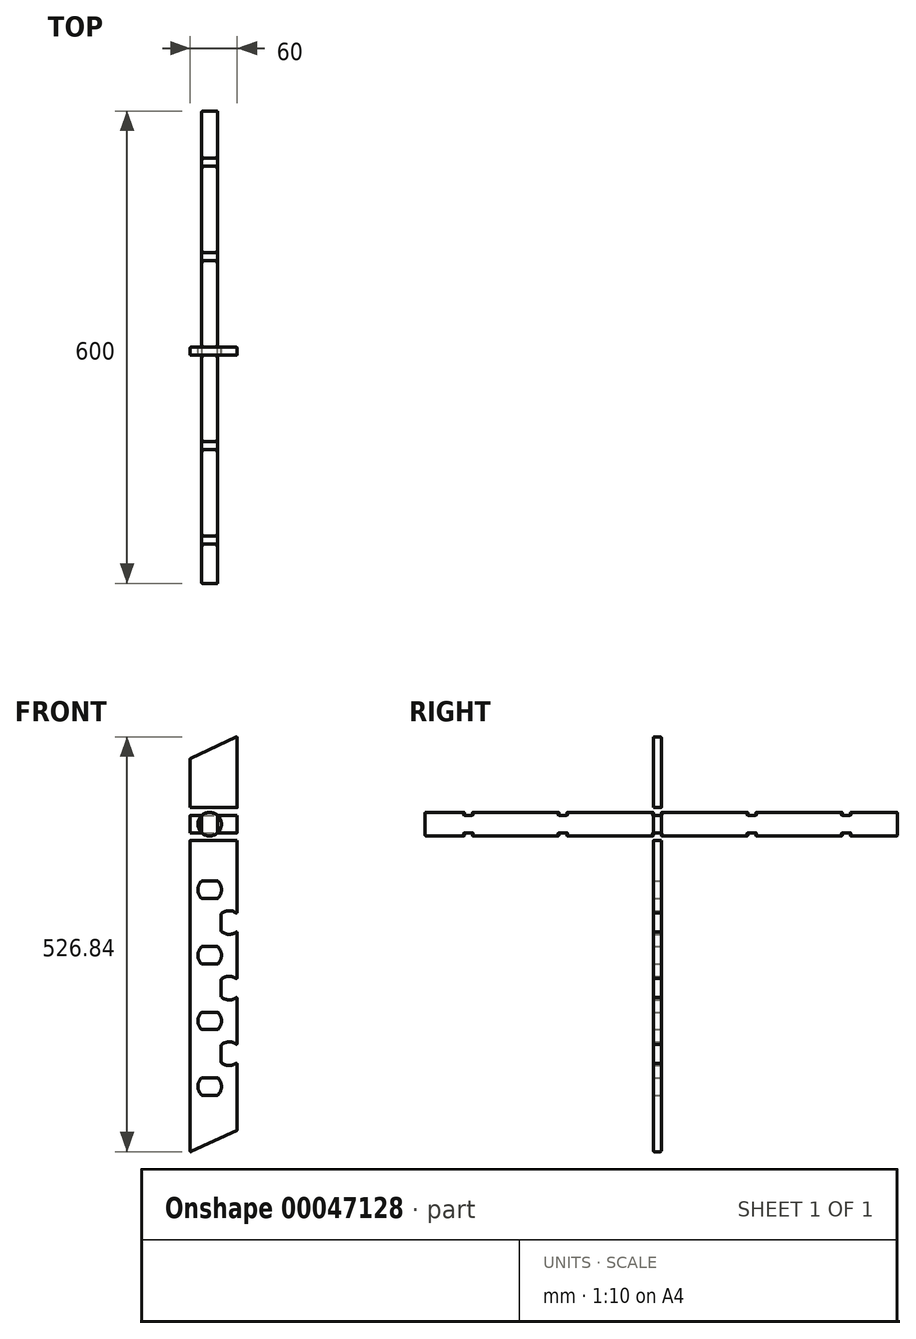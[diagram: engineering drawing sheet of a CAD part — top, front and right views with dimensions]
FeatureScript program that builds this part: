
annotation { "Feature Type Name" : "Feature", "Feature Type Description" : "" }
export const myFeature = defineFeature(function(context is Context, id is Id, definition is map)
    precondition{}
    {
        {
            var Q0;
            Q0=qCreatedBy(makeId("Front.planeOp"),FACE);
            var sketch = newSketch(context, id + "F0", { "sketchPlane" : qUnion([Q0])});
            skLineSegment(sketch, "E0.bottom", {"start": v(0, 0) * mm, "end": v(-60, 0) * mm, "construction": true});
            skLineSegment(sketch, "E0.left", {"start": v(0, 0) * mm, "end": v(0, 27.98) * mm, "construction": true});
            skLineSegment(sketch, "E1", {"start": v(0, 527.98) * mm, "end": v(-60, 500) * mm});
            skLineSegment(sketch, "E2", {"start": v(-60, 0) * mm, "end": v(0, 27.98) * mm});
            skLineSegment(sketch, "E3", {"start": v(0, 27.98) * mm, "end": v(0, 527.98) * mm});
            skLineSegment(sketch, "E4", {"start": v(-60, 500) * mm, "end": v(-60, 416.67) * mm});
            skLineSegment(sketch, "E5", {"start": v(-60, 250) * mm, "end": v(-60, 166.67) * mm});
            skLineSegment(sketch, "E6", {"start": v(-60, 83.33) * mm, "end": v(-60, 0) * mm});
            skLineSegment(sketch, "E7", {"start": v(-60, 166.67) * mm, "end": v(-60, 83.33) * mm});
            skLineSegment(sketch, "E8", {"start": v(-60, 333.33) * mm, "end": v(-60, 250) * mm});
            skLineSegment(sketch, "E9", {"start": v(-60, 416.67) * mm, "end": v(-60, 333.33) * mm});
            skLineSegment(sketch, "E10", {"start": v(-60, 416.67) * mm, "end": v(0, 416.67) * mm, "construction": true});
            skLineSegment(sketch, "E11", {"start": v(-60, 333.33) * mm, "end": v(0, 333.33) * mm, "construction": true});
            skLineSegment(sketch, "E12", {"start": v(-60, 250) * mm, "end": v(0, 250) * mm, "construction": true});
            skLineSegment(sketch, "E13", {"start": v(-60, 166.67) * mm, "end": v(0, 166.67) * mm, "construction": true});
            skLineSegment(sketch, "E14", {"start": v(-60, 83.33) * mm, "end": v(0, 83.33) * mm, "construction": true});
            skLineSegment(sketch, "E15", {"start": v(-35, 511.66) * mm, "end": v(-35, 11.66) * mm, "construction": true});
            skLineSegment(sketch, "E16", {"start": v(-45.2, 427.67) * mm, "end": v(-24.8, 427.67) * mm});
            skLineSegment(sketch, "E17", {"start": v(-24.8, 427.67) * mm, "end": v(-24.8, 405.67) * mm, "construction": true});
            skLineSegment(sketch, "E18", {"start": v(-24.8, 405.67) * mm, "end": v(-45.2, 405.67) * mm});
            skLineSegment(sketch, "E19", {"start": v(-45.2, 405.67) * mm, "end": v(-45.2, 427.67) * mm, "construction": true});
            skLineSegment(sketch, "E20", {"start": v(-45.2, 427.67) * mm, "end": v(-45.2, 427.67) * mm});
            skLineSegment(sketch, "E21", {"start": v(-45.2, 405.67) * mm, "end": v(-45.2, 405.67) * mm});
            skArc(sketch, "E22", {"start": v(-24.8, 405.67) * mm, "mid": v(-20, 416.67) * mm, "end": v(-24.8, 427.67) * mm});
            skArc(sketch, "E23", {"start": v(-45.2, 427.67) * mm, "mid": v(-50, 416.67) * mm, "end": v(-45.2, 405.67) * mm});
            skArc(sketch, "E24", {"start": v(-45.2, 427.67) * mm, "mid": v(-35, 431.67) * mm, "end": v(-24.8, 427.67) * mm, "construction": true});
            skArc(sketch, "E25", {"start": v(-24.8, 405.67) * mm, "mid": v(-35, 401.67) * mm, "end": v(-45.2, 405.67) * mm, "construction": true});
            skLineSegment(sketch, "E26", {"start": v(-45.2, 344.33) * mm, "end": v(-45.2, 344.33) * mm});
            skLineSegment(sketch, "E27", {"start": v(-45.2, 322.33) * mm, "end": v(-45.2, 344.33) * mm, "construction": true});
            skLineSegment(sketch, "E28", {"start": v(-24.8, 322.33) * mm, "end": v(-45.2, 322.33) * mm});
            skLineSegment(sketch, "E29", {"start": v(-45.2, 344.33) * mm, "end": v(-24.8, 344.33) * mm});
            skArc(sketch, "E30", {"start": v(-24.8, 322.33) * mm, "mid": v(-20, 333.33) * mm, "end": v(-24.8, 344.33) * mm});
            skArc(sketch, "E31", {"start": v(-24.8, 322.33) * mm, "mid": v(-35, 318.33) * mm, "end": v(-45.2, 322.33) * mm, "construction": true});
            skArc(sketch, "E32", {"start": v(-45.2, 344.33) * mm, "mid": v(-50, 333.33) * mm, "end": v(-45.2, 322.33) * mm});
            skLineSegment(sketch, "E33", {"start": v(-24.8, 344.33) * mm, "end": v(-24.8, 322.33) * mm, "construction": true});
            skArc(sketch, "E34", {"start": v(-45.2, 344.33) * mm, "mid": v(-35, 348.33) * mm, "end": v(-24.8, 344.33) * mm, "construction": true});
            skLineSegment(sketch, "E35", {"start": v(-45.2, 322.33) * mm, "end": v(-45.2, 322.33) * mm});
            skLineSegment(sketch, "E36", {"start": v(-45.2, 261) * mm, "end": v(-45.2, 261) * mm});
            skLineSegment(sketch, "E37", {"start": v(-45.2, 239) * mm, "end": v(-45.2, 261) * mm, "construction": true});
            skLineSegment(sketch, "E38", {"start": v(-24.8, 239) * mm, "end": v(-45.2, 239) * mm});
            skLineSegment(sketch, "E39", {"start": v(-45.2, 261) * mm, "end": v(-24.8, 261) * mm});
            skArc(sketch, "E40", {"start": v(-24.8, 239) * mm, "mid": v(-20, 250) * mm, "end": v(-24.8, 261) * mm});
            skArc(sketch, "E41", {"start": v(-24.8, 239) * mm, "mid": v(-35, 235) * mm, "end": v(-45.2, 239) * mm, "construction": true});
            skArc(sketch, "E42", {"start": v(-45.2, 261) * mm, "mid": v(-50, 250) * mm, "end": v(-45.2, 239) * mm});
            skLineSegment(sketch, "E43", {"start": v(-24.8, 261) * mm, "end": v(-24.8, 239) * mm, "construction": true});
            skArc(sketch, "E44", {"start": v(-45.2, 261) * mm, "mid": v(-35, 265) * mm, "end": v(-24.8, 261) * mm, "construction": true});
            skLineSegment(sketch, "E45", {"start": v(-45.2, 239) * mm, "end": v(-45.2, 239) * mm});
            skLineSegment(sketch, "E46", {"start": v(-45.2, 177.67) * mm, "end": v(-45.2, 177.67) * mm});
            skLineSegment(sketch, "E47", {"start": v(-45.2, 155.67) * mm, "end": v(-45.2, 177.67) * mm, "construction": true});
            skLineSegment(sketch, "E48", {"start": v(-24.8, 155.67) * mm, "end": v(-45.2, 155.67) * mm});
            skLineSegment(sketch, "E49", {"start": v(-45.2, 177.67) * mm, "end": v(-24.8, 177.67) * mm});
            skArc(sketch, "E50", {"start": v(-24.8, 155.67) * mm, "mid": v(-20, 166.67) * mm, "end": v(-24.8, 177.67) * mm});
            skArc(sketch, "E51", {"start": v(-24.8, 155.67) * mm, "mid": v(-35, 151.67) * mm, "end": v(-45.2, 155.67) * mm, "construction": true});
            skArc(sketch, "E52", {"start": v(-45.2, 177.67) * mm, "mid": v(-50, 166.67) * mm, "end": v(-45.2, 155.67) * mm});
            skLineSegment(sketch, "E53", {"start": v(-24.8, 177.67) * mm, "end": v(-24.8, 155.67) * mm, "construction": true});
            skArc(sketch, "E54", {"start": v(-45.2, 177.67) * mm, "mid": v(-35, 181.67) * mm, "end": v(-24.8, 177.67) * mm, "construction": true});
            skLineSegment(sketch, "E55", {"start": v(-45.2, 155.67) * mm, "end": v(-45.2, 155.67) * mm});
            skLineSegment(sketch, "E56", {"start": v(-45.2, 94.33) * mm, "end": v(-45.2, 94.33) * mm});
            skLineSegment(sketch, "E57", {"start": v(-45.2, 72.33) * mm, "end": v(-45.2, 94.33) * mm, "construction": true});
            skLineSegment(sketch, "E58", {"start": v(-24.8, 72.33) * mm, "end": v(-45.2, 72.33) * mm});
            skLineSegment(sketch, "E59", {"start": v(-45.2, 94.33) * mm, "end": v(-24.8, 94.33) * mm});
            skArc(sketch, "E60", {"start": v(-24.8, 72.33) * mm, "mid": v(-20, 83.33) * mm, "end": v(-24.8, 94.33) * mm});
            skArc(sketch, "E61", {"start": v(-24.8, 72.33) * mm, "mid": v(-35, 68.33) * mm, "end": v(-45.2, 72.33) * mm, "construction": true});
            skArc(sketch, "E62", {"start": v(-45.2, 94.33) * mm, "mid": v(-50, 83.33) * mm, "end": v(-45.2, 72.33) * mm});
            skLineSegment(sketch, "E63", {"start": v(-24.8, 94.33) * mm, "end": v(-24.8, 72.33) * mm, "construction": true});
            skArc(sketch, "E64", {"start": v(-45.2, 94.33) * mm, "mid": v(-35, 98.33) * mm, "end": v(-24.8, 94.33) * mm, "construction": true});
            skLineSegment(sketch, "E65", {"start": v(-45.2, 72.33) * mm, "end": v(-45.2, 72.33) * mm});
            skSolve(sketch);
        }
        {
            var Q0;
            Q0=qCreatedBy(makeId("Front.planeOp"),FACE);
            var sketch = newSketch(context, id + "F1", { "sketchPlane" : qUnion([Q0])});
            skLineSegment(sketch, "E66", {"start": v(-10.2, 208.33) * mm, "end": v(-35, 250) * mm, "construction": true});
            skLineSegment(sketch, "E67", {"start": v(-20.4, 219.33) * mm, "end": v(-20.4, 219.33) * mm});
            skLineSegment(sketch, "E68", {"start": v(-20.4, 219.33) * mm, "end": v(0, 219.33) * mm, "construction": true});
            skArc(sketch, "E69", {"start": v(-20.4, 219.33) * mm, "mid": v(-10.2, 223.33) * mm, "end": v(0, 219.33) * mm});
            skArc(sketch, "E70", {"start": v(0, 197.33) * mm, "mid": v(-10.2, 193.33) * mm, "end": v(-20.4, 197.33) * mm});
            skLineSegment(sketch, "E71", {"start": v(0, 197.33) * mm, "end": v(-20.4, 197.33) * mm, "construction": true});
            skLineSegment(sketch, "E72", {"start": v(-10.2, 208.33) * mm, "end": v(-35, 166.67) * mm, "construction": true});
            skLineSegment(sketch, "E73", {"start": v(-20.4, 197.33) * mm, "end": v(-20.4, 219.33) * mm});
            skArc(sketch, "E74", {"start": v(-20.4, 219.33) * mm, "mid": v(-25.2, 208.33) * mm, "end": v(-20.4, 197.33) * mm, "construction": true});
            skLineSegment(sketch, "E75", {"start": v(-20.4, 197.33) * mm, "end": v(-20.4, 197.33) * mm});
            skArc(sketch, "E76", {"start": v(0, 197.33) * mm, "mid": v(4.8, 208.33) * mm, "end": v(0, 219.33) * mm});
            skLineSegment(sketch, "E77", {"start": v(-10.2, 291.67) * mm, "end": v(-35, 333.33) * mm, "construction": true});
            skLineSegment(sketch, "E78", {"start": v(-20.4, 302.67) * mm, "end": v(-20.4, 302.67) * mm});
            skLineSegment(sketch, "E79", {"start": v(-20.4, 302.67) * mm, "end": v(0, 302.67) * mm, "construction": true});
            skArc(sketch, "E80", {"start": v(-20.4, 302.67) * mm, "mid": v(-10.2, 306.67) * mm, "end": v(0, 302.67) * mm});
            skArc(sketch, "E81", {"start": v(0, 280.67) * mm, "mid": v(-10.2, 276.67) * mm, "end": v(-20.4, 280.67) * mm});
            skLineSegment(sketch, "E82", {"start": v(0, 280.67) * mm, "end": v(-20.4, 280.67) * mm, "construction": true});
            skLineSegment(sketch, "E83", {"start": v(-10.2, 291.67) * mm, "end": v(-35, 250) * mm, "construction": true});
            skLineSegment(sketch, "E84", {"start": v(-20.4, 280.67) * mm, "end": v(-20.4, 302.67) * mm});
            skArc(sketch, "E85", {"start": v(-20.4, 302.67) * mm, "mid": v(-25.2, 291.67) * mm, "end": v(-20.4, 280.67) * mm, "construction": true});
            skLineSegment(sketch, "E86", {"start": v(-20.4, 280.67) * mm, "end": v(-20.4, 280.67) * mm});
            skArc(sketch, "E87", {"start": v(0, 280.67) * mm, "mid": v(4.8, 291.67) * mm, "end": v(0, 302.67) * mm});
            skLineSegment(sketch, "E88", {"start": v(-10.2, 125) * mm, "end": v(-35, 166.67) * mm, "construction": true});
            skLineSegment(sketch, "E89", {"start": v(-20.4, 136) * mm, "end": v(-20.4, 136) * mm});
            skLineSegment(sketch, "E90", {"start": v(-20.4, 136) * mm, "end": v(0, 136) * mm, "construction": true});
            skArc(sketch, "E91", {"start": v(-20.4, 136) * mm, "mid": v(-10.2, 140) * mm, "end": v(0, 136) * mm});
            skArc(sketch, "E92", {"start": v(0, 114) * mm, "mid": v(-10.2, 110) * mm, "end": v(-20.4, 114) * mm});
            skLineSegment(sketch, "E93", {"start": v(0, 114) * mm, "end": v(-20.4, 114) * mm, "construction": true});
            skLineSegment(sketch, "E94", {"start": v(-10.2, 125) * mm, "end": v(-35, 83.33) * mm, "construction": true});
            skLineSegment(sketch, "E95", {"start": v(-20.4, 114) * mm, "end": v(-20.4, 136) * mm});
            skArc(sketch, "E96", {"start": v(-20.4, 136) * mm, "mid": v(-25.2, 125) * mm, "end": v(-20.4, 114) * mm, "construction": true});
            skLineSegment(sketch, "E97", {"start": v(-20.4, 114) * mm, "end": v(-20.4, 114) * mm});
            skArc(sketch, "E98", {"start": v(0, 114) * mm, "mid": v(4.8, 125) * mm, "end": v(0, 136) * mm});
            skSolve(sketch);
        }
        {
            var Q0;
            Q0=makeQuery(id+"F0.imprint","IMPRINT",FACE,{"disambiguationData":[TD([[makeQuery(id+"F0.imprint","IMPRINT",EDGE,{"derivedFrom":sQuery(id+"F0.wireOp",EDGE,"E0.right")}),-1.0]])]});
            var Q1;
            Q1=makeQuery(id+"F0.imprint","IMPRINT",FACE,{"disambiguationData":[TD([[makeQuery(id+"F0.imprint","IMPRINT",EDGE,{"derivedFrom":sQuery(id+"F0.wireOp",EDGE,"E1")}),1.0]])]});
            extrude(context, id + "F2", {"entities" : qUnion([Q0, Q1]), "depth" : 10 * mm});
        }
        {
            var Q0;
            Q0 = qSketchRegion(id + "F1", true);
            extrude(context, id + "F3", {"entities" : qUnion([Q0]), "operationType" : NewBodyOperationType.REMOVE, "endBound" : BoundingType.THROUGH_ALL, "depth" : 25 * mm});
        }
        {
            var Q0;
            Q0=makeQuery(id+"F2.opExtrude","CAP_EDGE",EDGE,{"disambiguationData":[OSD([sQuery(id+"F0.wireOp",EDGE,"E30")])],"isStart":false});
            var Q1;
            Q1=makeQuery(id+"F2.opExtrude","CAP_EDGE",EDGE,{"disambiguationData":[OSD([sQuery(id+"F0.wireOp",EDGE,"E50")])],"isStart":false});
            var Q2;
            Q2=makeQuery(id+"F3.boolean.opBoolean","INTERSECT",EDGE,{"disambiguationData":[OD(0.0)],"derivedFrom":[makeQuery(id+"F2.opExtrude","SWEPT_FACE",FACE,{"disambiguationData":[OSD([sQuery(id+"F0.wireOp",EDGE,"E3")])]}),makeQuery(id+"F3.opExtrude","SWEPT_FACE",FACE,{"disambiguationData":[OSD([sQuery(id+"F1.wireOp",EDGE,"E69"),sQuery(id+"F1.wireOp",EDGE,"E70"),sQuery(id+"F1.wireOp",EDGE,"E76")])]})]});
            var Q3;
            Q3=makeQuery(id+"F3.boolean.opBoolean","INTERSECT",EDGE,{"disambiguationData":[OD(0.0)],"derivedFrom":[makeQuery(id+"F2.opExtrude","SWEPT_FACE",FACE,{"disambiguationData":[OSD([sQuery(id+"F0.wireOp",EDGE,"E3")])]}),makeQuery(id+"F3.opExtrude","SWEPT_FACE",FACE,{"disambiguationData":[OSD([sQuery(id+"F1.wireOp",EDGE,"E80"),sQuery(id+"F1.wireOp",EDGE,"E81"),sQuery(id+"F1.wireOp",EDGE,"E87")])]})]});
            var Q4;
            Q4=makeQuery(id+"F2.opExtrude","CAP_EDGE",EDGE,{"disambiguationData":[OSD([sQuery(id+"F0.wireOp",EDGE,"E29")])],"isStart":false});
            var Q5;
            Q5=makeQuery(id+"F2.opExtrude","CAP_EDGE",EDGE,{"disambiguationData":[OSD([sQuery(id+"F0.wireOp",EDGE,"E18")])],"isStart":false});
            var Q6;
            {var subQ0=sQuery(id+"F0.wireOp",EDGE,"E3");var subQ1=sQuery(id+"F0.wireOp",EDGE,"E1");Q6=makeQuery(id+"F3.boolean.opBoolean","SPLIT",EDGE,{"disambiguationData":[TD([makeQuery(id+"F2.opExtrude","SWEPT_FACE",FACE,{"disambiguationData":[OSD([subQ1])]}),makeQuery(id+"F2.opExtrude","CAP_FACE",FACE,{"disambiguationData":[OSD([subQ1,sQuery(id+"F0.wireOp",EDGE,"E2"),subQ0,sQuery(id+"F0.wireOp",EDGE,"E4"),sQuery(id+"F0.wireOp",EDGE,"E5"),sQuery(id+"F0.wireOp",EDGE,"E6"),sQuery(id+"F0.wireOp",EDGE,"E7"),sQuery(id+"F0.wireOp",EDGE,"E8"),sQuery(id+"F0.wireOp",EDGE,"E9"),sQuery(id+"F0.wireOp",EDGE,"E16"),sQuery(id+"F0.wireOp",EDGE,"E18"),sQuery(id+"F0.wireOp",EDGE,"E22"),sQuery(id+"F0.wireOp",EDGE,"E23"),sQuery(id+"F0.wireOp",EDGE,"E28"),sQuery(id+"F0.wireOp",EDGE,"E29"),sQuery(id+"F0.wireOp",EDGE,"E30"),sQuery(id+"F0.wireOp",EDGE,"E32"),sQuery(id+"F0.wireOp",EDGE,"E38"),sQuery(id+"F0.wireOp",EDGE,"E39"),sQuery(id+"F0.wireOp",EDGE,"E40"),sQuery(id+"F0.wireOp",EDGE,"E42"),sQuery(id+"F0.wireOp",EDGE,"E48"),sQuery(id+"F0.wireOp",EDGE,"E49"),sQuery(id+"F0.wireOp",EDGE,"E50"),sQuery(id+"F0.wireOp",EDGE,"E52"),sQuery(id+"F0.wireOp",EDGE,"E58"),sQuery(id+"F0.wireOp",EDGE,"E59"),sQuery(id+"F0.wireOp",EDGE,"E60"),sQuery(id+"F0.wireOp",EDGE,"E62")])],"isStart":true}),makeQuery(id+"F2.opExtrude","SWEPT_FACE",FACE,{"disambiguationData":[OSD([subQ0])]}),makeQuery(id+"F3.opExtrude","SWEPT_FACE",FACE,{"disambiguationData":[OSD([sQuery(id+"F1.wireOp",EDGE,"E80"),sQuery(id+"F1.wireOp",EDGE,"E81"),sQuery(id+"F1.wireOp",EDGE,"E87")])]})])],"derivedFrom":makeQuery(id+"F2.opExtrude","CAP_EDGE",EDGE,{"disambiguationData":[OSD([subQ0])],"isStart":true})});}
            var Q7;
            Q7=makeQuery(id+"F2.opExtrude","CAP_EDGE",EDGE,{"disambiguationData":[OSD([sQuery(id+"F0.wireOp",EDGE,"E39")])],"isStart":false});
            var Q8;
            {var subQ0=sQuery(id+"F0.wireOp",EDGE,"E3");Q8=makeQuery(id+"F3.boolean.opBoolean","SPLIT",EDGE,{"disambiguationData":[TD([makeQuery(id+"F2.opExtrude","CAP_FACE",FACE,{"disambiguationData":[OSD([sQuery(id+"F0.wireOp",EDGE,"E1"),sQuery(id+"F0.wireOp",EDGE,"E2"),subQ0,sQuery(id+"F0.wireOp",EDGE,"E4"),sQuery(id+"F0.wireOp",EDGE,"E5"),sQuery(id+"F0.wireOp",EDGE,"E6"),sQuery(id+"F0.wireOp",EDGE,"E7"),sQuery(id+"F0.wireOp",EDGE,"E8"),sQuery(id+"F0.wireOp",EDGE,"E9"),sQuery(id+"F0.wireOp",EDGE,"E16"),sQuery(id+"F0.wireOp",EDGE,"E18"),sQuery(id+"F0.wireOp",EDGE,"E22"),sQuery(id+"F0.wireOp",EDGE,"E23"),sQuery(id+"F0.wireOp",EDGE,"E28"),sQuery(id+"F0.wireOp",EDGE,"E29"),sQuery(id+"F0.wireOp",EDGE,"E30"),sQuery(id+"F0.wireOp",EDGE,"E32"),sQuery(id+"F0.wireOp",EDGE,"E38"),sQuery(id+"F0.wireOp",EDGE,"E39"),sQuery(id+"F0.wireOp",EDGE,"E40"),sQuery(id+"F0.wireOp",EDGE,"E42"),sQuery(id+"F0.wireOp",EDGE,"E48"),sQuery(id+"F0.wireOp",EDGE,"E49"),sQuery(id+"F0.wireOp",EDGE,"E50"),sQuery(id+"F0.wireOp",EDGE,"E52"),sQuery(id+"F0.wireOp",EDGE,"E58"),sQuery(id+"F0.wireOp",EDGE,"E59"),sQuery(id+"F0.wireOp",EDGE,"E60"),sQuery(id+"F0.wireOp",EDGE,"E62")])],"isStart":false}),makeQuery(id+"F2.opExtrude","SWEPT_FACE",FACE,{"disambiguationData":[OSD([subQ0])]}),makeQuery(id+"F3.opExtrude","SWEPT_FACE",FACE,{"disambiguationData":[OSD([sQuery(id+"F1.wireOp",EDGE,"E69"),sQuery(id+"F1.wireOp",EDGE,"E70"),sQuery(id+"F1.wireOp",EDGE,"E76")])]}),makeQuery(id+"F3.opExtrude","SWEPT_FACE",FACE,{"disambiguationData":[OSD([sQuery(id+"F1.wireOp",EDGE,"E80"),sQuery(id+"F1.wireOp",EDGE,"E81"),sQuery(id+"F1.wireOp",EDGE,"E87")])]})])],"derivedFrom":makeQuery(id+"F2.opExtrude","CAP_EDGE",EDGE,{"disambiguationData":[OSD([subQ0])],"isStart":false})});}
            var Q9;
            Q9=makeQuery(id+"F3.boolean.opBoolean","INTERSECT",EDGE,{"derivedFrom":[makeQuery(id+"F2.opExtrude","CAP_FACE",FACE,{"disambiguationData":[OSD([sQuery(id+"F0.wireOp",EDGE,"E1"),sQuery(id+"F0.wireOp",EDGE,"E2"),sQuery(id+"F0.wireOp",EDGE,"E3"),sQuery(id+"F0.wireOp",EDGE,"E4"),sQuery(id+"F0.wireOp",EDGE,"E5"),sQuery(id+"F0.wireOp",EDGE,"E6"),sQuery(id+"F0.wireOp",EDGE,"E7"),sQuery(id+"F0.wireOp",EDGE,"E8"),sQuery(id+"F0.wireOp",EDGE,"E9"),sQuery(id+"F0.wireOp",EDGE,"E16"),sQuery(id+"F0.wireOp",EDGE,"E18"),sQuery(id+"F0.wireOp",EDGE,"E22"),sQuery(id+"F0.wireOp",EDGE,"E23"),sQuery(id+"F0.wireOp",EDGE,"E28"),sQuery(id+"F0.wireOp",EDGE,"E29"),sQuery(id+"F0.wireOp",EDGE,"E30"),sQuery(id+"F0.wireOp",EDGE,"E32"),sQuery(id+"F0.wireOp",EDGE,"E38"),sQuery(id+"F0.wireOp",EDGE,"E39"),sQuery(id+"F0.wireOp",EDGE,"E40"),sQuery(id+"F0.wireOp",EDGE,"E42"),sQuery(id+"F0.wireOp",EDGE,"E48"),sQuery(id+"F0.wireOp",EDGE,"E49"),sQuery(id+"F0.wireOp",EDGE,"E50"),sQuery(id+"F0.wireOp",EDGE,"E52"),sQuery(id+"F0.wireOp",EDGE,"E58"),sQuery(id+"F0.wireOp",EDGE,"E59"),sQuery(id+"F0.wireOp",EDGE,"E60"),sQuery(id+"F0.wireOp",EDGE,"E62")])],"isStart":false}),makeQuery(id+"F3.opExtrude","SWEPT_FACE",FACE,{"disambiguationData":[OSD([sQuery(id+"F1.wireOp",EDGE,"E73")])]})]});
            var Q10;
            Q10=makeQuery(id+"F2.opExtrude","SWEPT_EDGE",EDGE,{"disambiguationData":[OSD([sQuery(id+"F0.wireOp",EDGE,"E2"),sQuery(id+"F0.wireOp",EDGE,"E6")])]});
            var Q11;
            Q11=makeQuery(id+"F2.opExtrude","SWEPT_EDGE",EDGE,{"disambiguationData":[OSD([sQuery(id+"F0.wireOp",EDGE,"E1"),sQuery(id+"F0.wireOp",EDGE,"E3")])]});
            var Q12;
            Q12=makeQuery(id+"F2.opExtrude","CAP_EDGE",EDGE,{"disambiguationData":[OSD([sQuery(id+"F0.wireOp",EDGE,"E1")])],"isStart":false});
            var Q13;
            Q13=makeQuery(id+"F2.opExtrude","CAP_EDGE",EDGE,{"disambiguationData":[OSD([sQuery(id+"F0.wireOp",EDGE,"E28")])],"isStart":false});
            var Q14;
            Q14=makeQuery(id+"F2.opExtrude","CAP_EDGE",EDGE,{"disambiguationData":[OSD([sQuery(id+"F0.wireOp",EDGE,"E16")])],"isStart":false});
            var Q15;
            Q15=makeQuery(id+"F2.opExtrude","CAP_EDGE",EDGE,{"disambiguationData":[OSD([sQuery(id+"F0.wireOp",EDGE,"E38")])],"isStart":false});
            var Q16;
            Q16=makeQuery(id+"F3.boolean.opBoolean","COPY",EDGE,{"disambiguationData":[OD(0.0)],"derivedFrom":makeQuery(id+"F3.opExtrude","CAP_EDGE",EDGE,{"disambiguationData":[OSD([sQuery(id+"F1.wireOp",EDGE,"E80"),sQuery(id+"F1.wireOp",EDGE,"E81"),sQuery(id+"F1.wireOp",EDGE,"E87")])],"isStart":true})});
            var Q17;
            Q17=makeQuery(id+"F2.opExtrude","CAP_EDGE",EDGE,{"disambiguationData":[OSD([sQuery(id+"F0.wireOp",EDGE,"E1")])],"isStart":true});
            var Q18;
            Q18=makeQuery(id+"F3.boolean.opBoolean","INTERSECT",EDGE,{"disambiguationData":[OD(1.0)],"derivedFrom":[makeQuery(id+"F2.opExtrude","CAP_FACE",FACE,{"disambiguationData":[OSD([sQuery(id+"F0.wireOp",EDGE,"E1"),sQuery(id+"F0.wireOp",EDGE,"E2"),sQuery(id+"F0.wireOp",EDGE,"E3"),sQuery(id+"F0.wireOp",EDGE,"E4"),sQuery(id+"F0.wireOp",EDGE,"E5"),sQuery(id+"F0.wireOp",EDGE,"E6"),sQuery(id+"F0.wireOp",EDGE,"E7"),sQuery(id+"F0.wireOp",EDGE,"E8"),sQuery(id+"F0.wireOp",EDGE,"E9"),sQuery(id+"F0.wireOp",EDGE,"E16"),sQuery(id+"F0.wireOp",EDGE,"E18"),sQuery(id+"F0.wireOp",EDGE,"E22"),sQuery(id+"F0.wireOp",EDGE,"E23"),sQuery(id+"F0.wireOp",EDGE,"E28"),sQuery(id+"F0.wireOp",EDGE,"E29"),sQuery(id+"F0.wireOp",EDGE,"E30"),sQuery(id+"F0.wireOp",EDGE,"E32"),sQuery(id+"F0.wireOp",EDGE,"E38"),sQuery(id+"F0.wireOp",EDGE,"E39"),sQuery(id+"F0.wireOp",EDGE,"E40"),sQuery(id+"F0.wireOp",EDGE,"E42"),sQuery(id+"F0.wireOp",EDGE,"E48"),sQuery(id+"F0.wireOp",EDGE,"E49"),sQuery(id+"F0.wireOp",EDGE,"E50"),sQuery(id+"F0.wireOp",EDGE,"E52"),sQuery(id+"F0.wireOp",EDGE,"E58"),sQuery(id+"F0.wireOp",EDGE,"E59"),sQuery(id+"F0.wireOp",EDGE,"E60"),sQuery(id+"F0.wireOp",EDGE,"E62")])],"isStart":false}),makeQuery(id+"F3.opExtrude","SWEPT_FACE",FACE,{"disambiguationData":[OSD([sQuery(id+"F1.wireOp",EDGE,"E80"),sQuery(id+"F1.wireOp",EDGE,"E81"),sQuery(id+"F1.wireOp",EDGE,"E87")])]})]});
            var Q19;
            Q19=makeQuery(id+"F2.opExtrude","CAP_EDGE",EDGE,{"disambiguationData":[OSD([sQuery(id+"F0.wireOp",EDGE,"E23")])],"isStart":false});
            var Q20;
            Q20=makeQuery(id+"F2.opExtrude","CAP_EDGE",EDGE,{"disambiguationData":[OSD([sQuery(id+"F0.wireOp",EDGE,"E42")])],"isStart":false});
            var Q21;
            Q21=makeQuery(id+"F3.boolean.opBoolean","INTERSECT",EDGE,{"disambiguationData":[OD(0.0)],"derivedFrom":[makeQuery(id+"F2.opExtrude","CAP_FACE",FACE,{"disambiguationData":[OSD([sQuery(id+"F0.wireOp",EDGE,"E1"),sQuery(id+"F0.wireOp",EDGE,"E2"),sQuery(id+"F0.wireOp",EDGE,"E3"),sQuery(id+"F0.wireOp",EDGE,"E4"),sQuery(id+"F0.wireOp",EDGE,"E5"),sQuery(id+"F0.wireOp",EDGE,"E6"),sQuery(id+"F0.wireOp",EDGE,"E7"),sQuery(id+"F0.wireOp",EDGE,"E8"),sQuery(id+"F0.wireOp",EDGE,"E9"),sQuery(id+"F0.wireOp",EDGE,"E16"),sQuery(id+"F0.wireOp",EDGE,"E18"),sQuery(id+"F0.wireOp",EDGE,"E22"),sQuery(id+"F0.wireOp",EDGE,"E23"),sQuery(id+"F0.wireOp",EDGE,"E28"),sQuery(id+"F0.wireOp",EDGE,"E29"),sQuery(id+"F0.wireOp",EDGE,"E30"),sQuery(id+"F0.wireOp",EDGE,"E32"),sQuery(id+"F0.wireOp",EDGE,"E38"),sQuery(id+"F0.wireOp",EDGE,"E39"),sQuery(id+"F0.wireOp",EDGE,"E40"),sQuery(id+"F0.wireOp",EDGE,"E42"),sQuery(id+"F0.wireOp",EDGE,"E48"),sQuery(id+"F0.wireOp",EDGE,"E49"),sQuery(id+"F0.wireOp",EDGE,"E50"),sQuery(id+"F0.wireOp",EDGE,"E52"),sQuery(id+"F0.wireOp",EDGE,"E58"),sQuery(id+"F0.wireOp",EDGE,"E59"),sQuery(id+"F0.wireOp",EDGE,"E60"),sQuery(id+"F0.wireOp",EDGE,"E62")])],"isStart":false}),makeQuery(id+"F3.opExtrude","SWEPT_FACE",FACE,{"disambiguationData":[OSD([sQuery(id+"F1.wireOp",EDGE,"E80"),sQuery(id+"F1.wireOp",EDGE,"E81"),sQuery(id+"F1.wireOp",EDGE,"E87")])]})]});
            var Q22;
            Q22=makeQuery(id+"F3.boolean.opBoolean","INTERSECT",EDGE,{"disambiguationData":[OD(1.0)],"derivedFrom":[makeQuery(id+"F2.opExtrude","CAP_FACE",FACE,{"disambiguationData":[OSD([sQuery(id+"F0.wireOp",EDGE,"E1"),sQuery(id+"F0.wireOp",EDGE,"E2"),sQuery(id+"F0.wireOp",EDGE,"E3"),sQuery(id+"F0.wireOp",EDGE,"E4"),sQuery(id+"F0.wireOp",EDGE,"E5"),sQuery(id+"F0.wireOp",EDGE,"E6"),sQuery(id+"F0.wireOp",EDGE,"E7"),sQuery(id+"F0.wireOp",EDGE,"E8"),sQuery(id+"F0.wireOp",EDGE,"E9"),sQuery(id+"F0.wireOp",EDGE,"E16"),sQuery(id+"F0.wireOp",EDGE,"E18"),sQuery(id+"F0.wireOp",EDGE,"E22"),sQuery(id+"F0.wireOp",EDGE,"E23"),sQuery(id+"F0.wireOp",EDGE,"E28"),sQuery(id+"F0.wireOp",EDGE,"E29"),sQuery(id+"F0.wireOp",EDGE,"E30"),sQuery(id+"F0.wireOp",EDGE,"E32"),sQuery(id+"F0.wireOp",EDGE,"E38"),sQuery(id+"F0.wireOp",EDGE,"E39"),sQuery(id+"F0.wireOp",EDGE,"E40"),sQuery(id+"F0.wireOp",EDGE,"E42"),sQuery(id+"F0.wireOp",EDGE,"E48"),sQuery(id+"F0.wireOp",EDGE,"E49"),sQuery(id+"F0.wireOp",EDGE,"E50"),sQuery(id+"F0.wireOp",EDGE,"E52"),sQuery(id+"F0.wireOp",EDGE,"E58"),sQuery(id+"F0.wireOp",EDGE,"E59"),sQuery(id+"F0.wireOp",EDGE,"E60"),sQuery(id+"F0.wireOp",EDGE,"E62")])],"isStart":false}),makeQuery(id+"F3.opExtrude","SWEPT_FACE",FACE,{"disambiguationData":[OSD([sQuery(id+"F1.wireOp",EDGE,"E69"),sQuery(id+"F1.wireOp",EDGE,"E70"),sQuery(id+"F1.wireOp",EDGE,"E76")])]})]});
            var Q23;
            Q23=makeQuery(id+"F3.boolean.opBoolean","COPY",EDGE,{"disambiguationData":[OD(0.0)],"derivedFrom":makeQuery(id+"F3.opExtrude","CAP_EDGE",EDGE,{"disambiguationData":[OSD([sQuery(id+"F1.wireOp",EDGE,"E69"),sQuery(id+"F1.wireOp",EDGE,"E70"),sQuery(id+"F1.wireOp",EDGE,"E76")])],"isStart":true})});
            var Q24;
            Q24=makeQuery(id+"F3.boolean.opBoolean","INTERSECT",EDGE,{"disambiguationData":[OD(1.0)],"derivedFrom":[makeQuery(id+"F2.opExtrude","SWEPT_FACE",FACE,{"disambiguationData":[OSD([sQuery(id+"F0.wireOp",EDGE,"E3")])]}),makeQuery(id+"F3.opExtrude","SWEPT_FACE",FACE,{"disambiguationData":[OSD([sQuery(id+"F1.wireOp",EDGE,"E80"),sQuery(id+"F1.wireOp",EDGE,"E81"),sQuery(id+"F1.wireOp",EDGE,"E87")])]})]});
            var Q25;
            Q25=makeQuery(id+"F2.opExtrude","CAP_EDGE",EDGE,{"disambiguationData":[OSD([sQuery(id+"F0.wireOp",EDGE,"E4"),sQuery(id+"F0.wireOp",EDGE,"E5"),sQuery(id+"F0.wireOp",EDGE,"E6"),sQuery(id+"F0.wireOp",EDGE,"E7"),sQuery(id+"F0.wireOp",EDGE,"E8"),sQuery(id+"F0.wireOp",EDGE,"E9")])],"isStart":false});
            var Q26;
            Q26=makeQuery(id+"F2.opExtrude","CAP_EDGE",EDGE,{"disambiguationData":[OSD([sQuery(id+"F0.wireOp",EDGE,"E32")])],"isStart":false});
            var Q27;
            Q27=makeQuery(id+"F2.opExtrude","CAP_EDGE",EDGE,{"disambiguationData":[OSD([sQuery(id+"F0.wireOp",EDGE,"E22")])],"isStart":false});
            var Q28;
            Q28=makeQuery(id+"F2.opExtrude","CAP_EDGE",EDGE,{"disambiguationData":[OSD([sQuery(id+"F0.wireOp",EDGE,"E4"),sQuery(id+"F0.wireOp",EDGE,"E5"),sQuery(id+"F0.wireOp",EDGE,"E6"),sQuery(id+"F0.wireOp",EDGE,"E7"),sQuery(id+"F0.wireOp",EDGE,"E8"),sQuery(id+"F0.wireOp",EDGE,"E9")])],"isStart":true});
            var Q29;
            Q29=makeQuery(id+"F2.opExtrude","CAP_EDGE",EDGE,{"disambiguationData":[OSD([sQuery(id+"F0.wireOp",EDGE,"E40")])],"isStart":false});
            var Q30;
            Q30=makeQuery(id+"F3.boolean.opBoolean","INTERSECT",EDGE,{"disambiguationData":[OD(0.0)],"derivedFrom":[makeQuery(id+"F2.opExtrude","CAP_FACE",FACE,{"disambiguationData":[OSD([sQuery(id+"F0.wireOp",EDGE,"E1"),sQuery(id+"F0.wireOp",EDGE,"E2"),sQuery(id+"F0.wireOp",EDGE,"E3"),sQuery(id+"F0.wireOp",EDGE,"E4"),sQuery(id+"F0.wireOp",EDGE,"E5"),sQuery(id+"F0.wireOp",EDGE,"E6"),sQuery(id+"F0.wireOp",EDGE,"E7"),sQuery(id+"F0.wireOp",EDGE,"E8"),sQuery(id+"F0.wireOp",EDGE,"E9"),sQuery(id+"F0.wireOp",EDGE,"E16"),sQuery(id+"F0.wireOp",EDGE,"E18"),sQuery(id+"F0.wireOp",EDGE,"E22"),sQuery(id+"F0.wireOp",EDGE,"E23"),sQuery(id+"F0.wireOp",EDGE,"E28"),sQuery(id+"F0.wireOp",EDGE,"E29"),sQuery(id+"F0.wireOp",EDGE,"E30"),sQuery(id+"F0.wireOp",EDGE,"E32"),sQuery(id+"F0.wireOp",EDGE,"E38"),sQuery(id+"F0.wireOp",EDGE,"E39"),sQuery(id+"F0.wireOp",EDGE,"E40"),sQuery(id+"F0.wireOp",EDGE,"E42"),sQuery(id+"F0.wireOp",EDGE,"E48"),sQuery(id+"F0.wireOp",EDGE,"E49"),sQuery(id+"F0.wireOp",EDGE,"E50"),sQuery(id+"F0.wireOp",EDGE,"E52"),sQuery(id+"F0.wireOp",EDGE,"E58"),sQuery(id+"F0.wireOp",EDGE,"E59"),sQuery(id+"F0.wireOp",EDGE,"E60"),sQuery(id+"F0.wireOp",EDGE,"E62")])],"isStart":false}),makeQuery(id+"F3.opExtrude","SWEPT_FACE",FACE,{"disambiguationData":[OSD([sQuery(id+"F1.wireOp",EDGE,"E69"),sQuery(id+"F1.wireOp",EDGE,"E70"),sQuery(id+"F1.wireOp",EDGE,"E76")])]})]});
            var Q31;
            Q31=makeQuery(id+"F3.boolean.opBoolean","INTERSECT",EDGE,{"disambiguationData":[OD(1.0)],"derivedFrom":[makeQuery(id+"F2.opExtrude","SWEPT_FACE",FACE,{"disambiguationData":[OSD([sQuery(id+"F0.wireOp",EDGE,"E3")])]}),makeQuery(id+"F3.opExtrude","SWEPT_FACE",FACE,{"disambiguationData":[OSD([sQuery(id+"F1.wireOp",EDGE,"E69"),sQuery(id+"F1.wireOp",EDGE,"E70"),sQuery(id+"F1.wireOp",EDGE,"E76")])]})]});
            var Q32;
            Q32=makeQuery(id+"F2.opExtrude","CAP_EDGE",EDGE,{"disambiguationData":[OSD([sQuery(id+"F0.wireOp",EDGE,"E22")])],"isStart":true});
            var Q33;
            Q33=makeQuery(id+"F2.opExtrude","CAP_EDGE",EDGE,{"disambiguationData":[OSD([sQuery(id+"F0.wireOp",EDGE,"E40")])],"isStart":true});
            var Q34;
            Q34=makeQuery(id+"F2.opExtrude","CAP_EDGE",EDGE,{"disambiguationData":[OSD([sQuery(id+"F0.wireOp",EDGE,"E60")])],"isStart":true});
            var Q35;
            {var subQ0=sQuery(id+"F0.wireOp",EDGE,"E3");Q35=makeQuery(id+"F3.boolean.opBoolean","SPLIT",EDGE,{"disambiguationData":[TD([makeQuery(id+"F2.opExtrude","CAP_FACE",FACE,{"disambiguationData":[OSD([sQuery(id+"F0.wireOp",EDGE,"E1"),sQuery(id+"F0.wireOp",EDGE,"E2"),subQ0,sQuery(id+"F0.wireOp",EDGE,"E4"),sQuery(id+"F0.wireOp",EDGE,"E5"),sQuery(id+"F0.wireOp",EDGE,"E6"),sQuery(id+"F0.wireOp",EDGE,"E7"),sQuery(id+"F0.wireOp",EDGE,"E8"),sQuery(id+"F0.wireOp",EDGE,"E9"),sQuery(id+"F0.wireOp",EDGE,"E16"),sQuery(id+"F0.wireOp",EDGE,"E18"),sQuery(id+"F0.wireOp",EDGE,"E22"),sQuery(id+"F0.wireOp",EDGE,"E23"),sQuery(id+"F0.wireOp",EDGE,"E28"),sQuery(id+"F0.wireOp",EDGE,"E29"),sQuery(id+"F0.wireOp",EDGE,"E30"),sQuery(id+"F0.wireOp",EDGE,"E32"),sQuery(id+"F0.wireOp",EDGE,"E38"),sQuery(id+"F0.wireOp",EDGE,"E39"),sQuery(id+"F0.wireOp",EDGE,"E40"),sQuery(id+"F0.wireOp",EDGE,"E42"),sQuery(id+"F0.wireOp",EDGE,"E48"),sQuery(id+"F0.wireOp",EDGE,"E49"),sQuery(id+"F0.wireOp",EDGE,"E50"),sQuery(id+"F0.wireOp",EDGE,"E52"),sQuery(id+"F0.wireOp",EDGE,"E58"),sQuery(id+"F0.wireOp",EDGE,"E59"),sQuery(id+"F0.wireOp",EDGE,"E60"),sQuery(id+"F0.wireOp",EDGE,"E62")])],"isStart":false}),makeQuery(id+"F2.opExtrude","SWEPT_FACE",FACE,{"disambiguationData":[OSD([subQ0])]}),makeQuery(id+"F3.opExtrude","SWEPT_FACE",FACE,{"disambiguationData":[OSD([sQuery(id+"F1.wireOp",EDGE,"E69"),sQuery(id+"F1.wireOp",EDGE,"E70"),sQuery(id+"F1.wireOp",EDGE,"E76")])]}),makeQuery(id+"F3.opExtrude","SWEPT_FACE",FACE,{"disambiguationData":[OSD([sQuery(id+"F1.wireOp",EDGE,"E91"),sQuery(id+"F1.wireOp",EDGE,"E92"),sQuery(id+"F1.wireOp",EDGE,"E98")])]})])],"derivedFrom":makeQuery(id+"F2.opExtrude","CAP_EDGE",EDGE,{"disambiguationData":[OSD([subQ0])],"isStart":false})});}
            var Q36;
            Q36=makeQuery(id+"F2.opExtrude","CAP_EDGE",EDGE,{"disambiguationData":[OSD([sQuery(id+"F0.wireOp",EDGE,"E2")])],"isStart":false});
            var Q37;
            Q37=makeQuery(id+"F2.opExtrude","CAP_EDGE",EDGE,{"disambiguationData":[OSD([sQuery(id+"F0.wireOp",EDGE,"E49")])],"isStart":false});
            var Q38;
            Q38=makeQuery(id+"F2.opExtrude","CAP_EDGE",EDGE,{"disambiguationData":[OSD([sQuery(id+"F0.wireOp",EDGE,"E59")])],"isStart":false});
            var Q39;
            Q39=makeQuery(id+"F2.opExtrude","SWEPT_EDGE",EDGE,{"disambiguationData":[OSD([sQuery(id+"F0.wireOp",EDGE,"E49"),sQuery(id+"F0.wireOp",EDGE,"E50")])]});
            var Q40;
            Q40=makeQuery(id+"F3.boolean.opBoolean","INTERSECT",EDGE,{"derivedFrom":[makeQuery(id+"F2.opExtrude","CAP_FACE",FACE,{"disambiguationData":[OSD([sQuery(id+"F0.wireOp",EDGE,"E1"),sQuery(id+"F0.wireOp",EDGE,"E2"),sQuery(id+"F0.wireOp",EDGE,"E3"),sQuery(id+"F0.wireOp",EDGE,"E4"),sQuery(id+"F0.wireOp",EDGE,"E5"),sQuery(id+"F0.wireOp",EDGE,"E6"),sQuery(id+"F0.wireOp",EDGE,"E7"),sQuery(id+"F0.wireOp",EDGE,"E8"),sQuery(id+"F0.wireOp",EDGE,"E9"),sQuery(id+"F0.wireOp",EDGE,"E16"),sQuery(id+"F0.wireOp",EDGE,"E18"),sQuery(id+"F0.wireOp",EDGE,"E22"),sQuery(id+"F0.wireOp",EDGE,"E23"),sQuery(id+"F0.wireOp",EDGE,"E28"),sQuery(id+"F0.wireOp",EDGE,"E29"),sQuery(id+"F0.wireOp",EDGE,"E30"),sQuery(id+"F0.wireOp",EDGE,"E32"),sQuery(id+"F0.wireOp",EDGE,"E38"),sQuery(id+"F0.wireOp",EDGE,"E39"),sQuery(id+"F0.wireOp",EDGE,"E40"),sQuery(id+"F0.wireOp",EDGE,"E42"),sQuery(id+"F0.wireOp",EDGE,"E48"),sQuery(id+"F0.wireOp",EDGE,"E49"),sQuery(id+"F0.wireOp",EDGE,"E50"),sQuery(id+"F0.wireOp",EDGE,"E52"),sQuery(id+"F0.wireOp",EDGE,"E58"),sQuery(id+"F0.wireOp",EDGE,"E59"),sQuery(id+"F0.wireOp",EDGE,"E60"),sQuery(id+"F0.wireOp",EDGE,"E62")])],"isStart":false}),makeQuery(id+"F3.opExtrude","SWEPT_FACE",FACE,{"disambiguationData":[OSD([sQuery(id+"F1.wireOp",EDGE,"E84")])]})]});
            var Q41;
            Q41=makeQuery(id+"F3.boolean.opBoolean","COPY",EDGE,{"derivedFrom":makeQuery(id+"F3.opExtrude","CAP_EDGE",EDGE,{"disambiguationData":[OSD([sQuery(id+"F1.wireOp",EDGE,"E84")])],"isStart":true})});
            var Q42;
            Q42=makeQuery(id+"F3.boolean.opBoolean","COPY",EDGE,{"derivedFrom":makeQuery(id+"F3.opExtrude","CAP_EDGE",EDGE,{"disambiguationData":[OSD([sQuery(id+"F1.wireOp",EDGE,"E73")])],"isStart":true})});
            var Q43;
            Q43=makeQuery(id+"F2.opExtrude","CAP_EDGE",EDGE,{"disambiguationData":[OSD([sQuery(id+"F0.wireOp",EDGE,"E2")])],"isStart":true});
            var Q44;
            Q44=makeQuery(id+"F2.opExtrude","CAP_EDGE",EDGE,{"disambiguationData":[OSD([sQuery(id+"F0.wireOp",EDGE,"E29")])],"isStart":true});
            var Q45;
            Q45=makeQuery(id+"F3.boolean.opBoolean","COPY",EDGE,{"derivedFrom":makeQuery(id+"F3.opExtrude","SWEPT_EDGE",EDGE,{"disambiguationData":[OSD([sQuery(id+"F1.wireOp",EDGE,"E81"),sQuery(id+"F1.wireOp",EDGE,"E84")])]})});
            var Q46;
            Q46=makeQuery(id+"F3.boolean.opBoolean","INTERSECT",EDGE,{"disambiguationData":[OD(1.0)],"derivedFrom":[makeQuery(id+"F2.opExtrude","CAP_FACE",FACE,{"disambiguationData":[OSD([sQuery(id+"F0.wireOp",EDGE,"E1"),sQuery(id+"F0.wireOp",EDGE,"E2"),sQuery(id+"F0.wireOp",EDGE,"E3"),sQuery(id+"F0.wireOp",EDGE,"E4"),sQuery(id+"F0.wireOp",EDGE,"E5"),sQuery(id+"F0.wireOp",EDGE,"E6"),sQuery(id+"F0.wireOp",EDGE,"E7"),sQuery(id+"F0.wireOp",EDGE,"E8"),sQuery(id+"F0.wireOp",EDGE,"E9"),sQuery(id+"F0.wireOp",EDGE,"E16"),sQuery(id+"F0.wireOp",EDGE,"E18"),sQuery(id+"F0.wireOp",EDGE,"E22"),sQuery(id+"F0.wireOp",EDGE,"E23"),sQuery(id+"F0.wireOp",EDGE,"E28"),sQuery(id+"F0.wireOp",EDGE,"E29"),sQuery(id+"F0.wireOp",EDGE,"E30"),sQuery(id+"F0.wireOp",EDGE,"E32"),sQuery(id+"F0.wireOp",EDGE,"E38"),sQuery(id+"F0.wireOp",EDGE,"E39"),sQuery(id+"F0.wireOp",EDGE,"E40"),sQuery(id+"F0.wireOp",EDGE,"E42"),sQuery(id+"F0.wireOp",EDGE,"E48"),sQuery(id+"F0.wireOp",EDGE,"E49"),sQuery(id+"F0.wireOp",EDGE,"E50"),sQuery(id+"F0.wireOp",EDGE,"E52"),sQuery(id+"F0.wireOp",EDGE,"E58"),sQuery(id+"F0.wireOp",EDGE,"E59"),sQuery(id+"F0.wireOp",EDGE,"E60"),sQuery(id+"F0.wireOp",EDGE,"E62")])],"isStart":false}),makeQuery(id+"F3.opExtrude","SWEPT_FACE",FACE,{"disambiguationData":[OSD([sQuery(id+"F1.wireOp",EDGE,"E91"),sQuery(id+"F1.wireOp",EDGE,"E92"),sQuery(id+"F1.wireOp",EDGE,"E98")])]})]});
            var Q47;
            Q47=makeQuery(id+"F3.boolean.opBoolean","COPY",EDGE,{"derivedFrom":makeQuery(id+"F3.opExtrude","SWEPT_EDGE",EDGE,{"disambiguationData":[OSD([sQuery(id+"F1.wireOp",EDGE,"E80"),sQuery(id+"F1.wireOp",EDGE,"E84")])]})});
            var Q48;
            Q48=makeQuery(id+"F3.boolean.opBoolean","COPY",EDGE,{"derivedFrom":makeQuery(id+"F3.opExtrude","SWEPT_EDGE",EDGE,{"disambiguationData":[OSD([sQuery(id+"F1.wireOp",EDGE,"E70"),sQuery(id+"F1.wireOp",EDGE,"E73")])]})});
            var Q49;
            Q49=makeQuery(id+"F2.opExtrude","SWEPT_EDGE",EDGE,{"disambiguationData":[OSD([sQuery(id+"F0.wireOp",EDGE,"E38"),sQuery(id+"F0.wireOp",EDGE,"E40")])]});
            var Q50;
            Q50=makeQuery(id+"F3.boolean.opBoolean","COPY",EDGE,{"derivedFrom":makeQuery(id+"F3.opExtrude","SWEPT_EDGE",EDGE,{"disambiguationData":[OSD([sQuery(id+"F1.wireOp",EDGE,"E69"),sQuery(id+"F1.wireOp",EDGE,"E73")])]})});
            var Q51;
            {var subQ0=sQuery(id+"F0.wireOp",EDGE,"E3");var subQ1=sQuery(id+"F0.wireOp",EDGE,"E2");Q51=makeQuery(id+"F3.boolean.opBoolean","SPLIT",EDGE,{"disambiguationData":[TD([makeQuery(id+"F2.opExtrude","CAP_FACE",FACE,{"disambiguationData":[OSD([sQuery(id+"F0.wireOp",EDGE,"E1"),subQ1,subQ0,sQuery(id+"F0.wireOp",EDGE,"E4"),sQuery(id+"F0.wireOp",EDGE,"E5"),sQuery(id+"F0.wireOp",EDGE,"E6"),sQuery(id+"F0.wireOp",EDGE,"E7"),sQuery(id+"F0.wireOp",EDGE,"E8"),sQuery(id+"F0.wireOp",EDGE,"E9"),sQuery(id+"F0.wireOp",EDGE,"E16"),sQuery(id+"F0.wireOp",EDGE,"E18"),sQuery(id+"F0.wireOp",EDGE,"E22"),sQuery(id+"F0.wireOp",EDGE,"E23"),sQuery(id+"F0.wireOp",EDGE,"E28"),sQuery(id+"F0.wireOp",EDGE,"E29"),sQuery(id+"F0.wireOp",EDGE,"E30"),sQuery(id+"F0.wireOp",EDGE,"E32"),sQuery(id+"F0.wireOp",EDGE,"E38"),sQuery(id+"F0.wireOp",EDGE,"E39"),sQuery(id+"F0.wireOp",EDGE,"E40"),sQuery(id+"F0.wireOp",EDGE,"E42"),sQuery(id+"F0.wireOp",EDGE,"E48"),sQuery(id+"F0.wireOp",EDGE,"E49"),sQuery(id+"F0.wireOp",EDGE,"E50"),sQuery(id+"F0.wireOp",EDGE,"E52"),sQuery(id+"F0.wireOp",EDGE,"E58"),sQuery(id+"F0.wireOp",EDGE,"E59"),sQuery(id+"F0.wireOp",EDGE,"E60"),sQuery(id+"F0.wireOp",EDGE,"E62")])],"isStart":false}),makeQuery(id+"F2.opExtrude","SWEPT_FACE",FACE,{"disambiguationData":[OSD([subQ1])]}),makeQuery(id+"F2.opExtrude","SWEPT_FACE",FACE,{"disambiguationData":[OSD([subQ0])]}),makeQuery(id+"F3.opExtrude","SWEPT_FACE",FACE,{"disambiguationData":[OSD([sQuery(id+"F1.wireOp",EDGE,"E91"),sQuery(id+"F1.wireOp",EDGE,"E92"),sQuery(id+"F1.wireOp",EDGE,"E98")])]})])],"derivedFrom":makeQuery(id+"F2.opExtrude","CAP_EDGE",EDGE,{"disambiguationData":[OSD([subQ0])],"isStart":false})});}
            var Q52;
            Q52=makeQuery(id+"F2.opExtrude","SWEPT_EDGE",EDGE,{"disambiguationData":[OSD([sQuery(id+"F0.wireOp",EDGE,"E29"),sQuery(id+"F0.wireOp",EDGE,"E30")])]});
            var Q53;
            {var subQ0=sQuery(id+"F0.wireOp",EDGE,"E3");var subQ1=sQuery(id+"F0.wireOp",EDGE,"E1");Q53=makeQuery(id+"F3.boolean.opBoolean","SPLIT",EDGE,{"disambiguationData":[TD([makeQuery(id+"F2.opExtrude","SWEPT_FACE",FACE,{"disambiguationData":[OSD([subQ1])]}),makeQuery(id+"F2.opExtrude","CAP_FACE",FACE,{"disambiguationData":[OSD([subQ1,sQuery(id+"F0.wireOp",EDGE,"E2"),subQ0,sQuery(id+"F0.wireOp",EDGE,"E4"),sQuery(id+"F0.wireOp",EDGE,"E5"),sQuery(id+"F0.wireOp",EDGE,"E6"),sQuery(id+"F0.wireOp",EDGE,"E7"),sQuery(id+"F0.wireOp",EDGE,"E8"),sQuery(id+"F0.wireOp",EDGE,"E9"),sQuery(id+"F0.wireOp",EDGE,"E16"),sQuery(id+"F0.wireOp",EDGE,"E18"),sQuery(id+"F0.wireOp",EDGE,"E22"),sQuery(id+"F0.wireOp",EDGE,"E23"),sQuery(id+"F0.wireOp",EDGE,"E28"),sQuery(id+"F0.wireOp",EDGE,"E29"),sQuery(id+"F0.wireOp",EDGE,"E30"),sQuery(id+"F0.wireOp",EDGE,"E32"),sQuery(id+"F0.wireOp",EDGE,"E38"),sQuery(id+"F0.wireOp",EDGE,"E39"),sQuery(id+"F0.wireOp",EDGE,"E40"),sQuery(id+"F0.wireOp",EDGE,"E42"),sQuery(id+"F0.wireOp",EDGE,"E48"),sQuery(id+"F0.wireOp",EDGE,"E49"),sQuery(id+"F0.wireOp",EDGE,"E50"),sQuery(id+"F0.wireOp",EDGE,"E52"),sQuery(id+"F0.wireOp",EDGE,"E58"),sQuery(id+"F0.wireOp",EDGE,"E59"),sQuery(id+"F0.wireOp",EDGE,"E60"),sQuery(id+"F0.wireOp",EDGE,"E62")])],"isStart":false}),makeQuery(id+"F2.opExtrude","SWEPT_FACE",FACE,{"disambiguationData":[OSD([subQ0])]}),makeQuery(id+"F3.opExtrude","SWEPT_FACE",FACE,{"disambiguationData":[OSD([sQuery(id+"F1.wireOp",EDGE,"E80"),sQuery(id+"F1.wireOp",EDGE,"E81"),sQuery(id+"F1.wireOp",EDGE,"E87")])]})])],"derivedFrom":makeQuery(id+"F2.opExtrude","CAP_EDGE",EDGE,{"disambiguationData":[OSD([subQ0])],"isStart":false})});}
            var Q54;
            Q54=makeQuery(id+"F2.opExtrude","SWEPT_EDGE",EDGE,{"disambiguationData":[OSD([sQuery(id+"F0.wireOp",EDGE,"E29"),sQuery(id+"F0.wireOp",EDGE,"E32")])]});
            var Q55;
            Q55=makeQuery(id+"F2.opExtrude","SWEPT_EDGE",EDGE,{"disambiguationData":[OSD([sQuery(id+"F0.wireOp",EDGE,"E28"),sQuery(id+"F0.wireOp",EDGE,"E32")])]});
            var Q56;
            Q56=makeQuery(id+"F2.opExtrude","SWEPT_EDGE",EDGE,{"disambiguationData":[OSD([sQuery(id+"F0.wireOp",EDGE,"E28"),sQuery(id+"F0.wireOp",EDGE,"E30")])]});
            var Q57;
            Q57=makeQuery(id+"F2.opExtrude","SWEPT_EDGE",EDGE,{"disambiguationData":[OSD([sQuery(id+"F0.wireOp",EDGE,"E18"),sQuery(id+"F0.wireOp",EDGE,"E23")])]});
            var Q58;
            Q58=makeQuery(id+"F2.opExtrude","SWEPT_EDGE",EDGE,{"disambiguationData":[OSD([sQuery(id+"F0.wireOp",EDGE,"E18"),sQuery(id+"F0.wireOp",EDGE,"E22")])]});
            var Q59;
            Q59=makeQuery(id+"F2.opExtrude","SWEPT_EDGE",EDGE,{"disambiguationData":[OSD([sQuery(id+"F0.wireOp",EDGE,"E16"),sQuery(id+"F0.wireOp",EDGE,"E22")])]});
            var Q60;
            Q60=makeQuery(id+"F2.opExtrude","SWEPT_EDGE",EDGE,{"disambiguationData":[OSD([sQuery(id+"F0.wireOp",EDGE,"E16"),sQuery(id+"F0.wireOp",EDGE,"E23")])]});
            var Q61;
            Q61=makeQuery(id+"F2.opExtrude","SWEPT_EDGE",EDGE,{"disambiguationData":[OSD([sQuery(id+"F0.wireOp",EDGE,"E2"),sQuery(id+"F0.wireOp",EDGE,"E3")])]});
            var Q62;
            Q62=makeQuery(id+"F2.opExtrude","SWEPT_EDGE",EDGE,{"disambiguationData":[OSD([sQuery(id+"F0.wireOp",EDGE,"E1"),sQuery(id+"F0.wireOp",EDGE,"E4")])]});
            var Q63;
            Q63=makeQuery(id+"F2.opExtrude","CAP_EDGE",EDGE,{"disambiguationData":[OSD([sQuery(id+"F0.wireOp",EDGE,"E18")])],"isStart":true});
            var Q64;
            Q64=makeQuery(id+"F2.opExtrude","CAP_EDGE",EDGE,{"disambiguationData":[OSD([sQuery(id+"F0.wireOp",EDGE,"E39")])],"isStart":true});
            var Q65;
            Q65=makeQuery(id+"F2.opExtrude","SWEPT_EDGE",EDGE,{"disambiguationData":[OSD([sQuery(id+"F0.wireOp",EDGE,"E39"),sQuery(id+"F0.wireOp",EDGE,"E40")])]});
            var Q66;
            {var subQ0=sQuery(id+"F0.wireOp",EDGE,"E3");Q66=makeQuery(id+"F3.boolean.opBoolean","SPLIT",EDGE,{"disambiguationData":[TD([makeQuery(id+"F2.opExtrude","CAP_FACE",FACE,{"disambiguationData":[OSD([sQuery(id+"F0.wireOp",EDGE,"E1"),sQuery(id+"F0.wireOp",EDGE,"E2"),subQ0,sQuery(id+"F0.wireOp",EDGE,"E4"),sQuery(id+"F0.wireOp",EDGE,"E5"),sQuery(id+"F0.wireOp",EDGE,"E6"),sQuery(id+"F0.wireOp",EDGE,"E7"),sQuery(id+"F0.wireOp",EDGE,"E8"),sQuery(id+"F0.wireOp",EDGE,"E9"),sQuery(id+"F0.wireOp",EDGE,"E16"),sQuery(id+"F0.wireOp",EDGE,"E18"),sQuery(id+"F0.wireOp",EDGE,"E22"),sQuery(id+"F0.wireOp",EDGE,"E23"),sQuery(id+"F0.wireOp",EDGE,"E28"),sQuery(id+"F0.wireOp",EDGE,"E29"),sQuery(id+"F0.wireOp",EDGE,"E30"),sQuery(id+"F0.wireOp",EDGE,"E32"),sQuery(id+"F0.wireOp",EDGE,"E38"),sQuery(id+"F0.wireOp",EDGE,"E39"),sQuery(id+"F0.wireOp",EDGE,"E40"),sQuery(id+"F0.wireOp",EDGE,"E42"),sQuery(id+"F0.wireOp",EDGE,"E48"),sQuery(id+"F0.wireOp",EDGE,"E49"),sQuery(id+"F0.wireOp",EDGE,"E50"),sQuery(id+"F0.wireOp",EDGE,"E52"),sQuery(id+"F0.wireOp",EDGE,"E58"),sQuery(id+"F0.wireOp",EDGE,"E59"),sQuery(id+"F0.wireOp",EDGE,"E60"),sQuery(id+"F0.wireOp",EDGE,"E62")])],"isStart":true}),makeQuery(id+"F2.opExtrude","SWEPT_FACE",FACE,{"disambiguationData":[OSD([subQ0])]}),makeQuery(id+"F3.opExtrude","SWEPT_FACE",FACE,{"disambiguationData":[OSD([sQuery(id+"F1.wireOp",EDGE,"E69"),sQuery(id+"F1.wireOp",EDGE,"E70"),sQuery(id+"F1.wireOp",EDGE,"E76")])]}),makeQuery(id+"F3.opExtrude","SWEPT_FACE",FACE,{"disambiguationData":[OSD([sQuery(id+"F1.wireOp",EDGE,"E91"),sQuery(id+"F1.wireOp",EDGE,"E92"),sQuery(id+"F1.wireOp",EDGE,"E98")])]})])],"derivedFrom":makeQuery(id+"F2.opExtrude","CAP_EDGE",EDGE,{"disambiguationData":[OSD([subQ0])],"isStart":true})});}
            var Q67;
            Q67=makeQuery(id+"F3.boolean.opBoolean","COPY",EDGE,{"disambiguationData":[OD(1.0)],"derivedFrom":makeQuery(id+"F3.opExtrude","CAP_EDGE",EDGE,{"disambiguationData":[OSD([sQuery(id+"F1.wireOp",EDGE,"E80"),sQuery(id+"F1.wireOp",EDGE,"E81"),sQuery(id+"F1.wireOp",EDGE,"E87")])],"isStart":true})});
            var Q68;
            Q68=makeQuery(id+"F2.opExtrude","SWEPT_EDGE",EDGE,{"disambiguationData":[OSD([sQuery(id+"F0.wireOp",EDGE,"E39"),sQuery(id+"F0.wireOp",EDGE,"E42")])]});
            var Q69;
            Q69=makeQuery(id+"F2.opExtrude","SWEPT_EDGE",EDGE,{"disambiguationData":[OSD([sQuery(id+"F0.wireOp",EDGE,"E38"),sQuery(id+"F0.wireOp",EDGE,"E42")])]});
            var Q70;
            Q70=makeQuery(id+"F3.boolean.opBoolean","INTERSECT",EDGE,{"disambiguationData":[OD(0.0)],"derivedFrom":[makeQuery(id+"F2.opExtrude","CAP_FACE",FACE,{"disambiguationData":[OSD([sQuery(id+"F0.wireOp",EDGE,"E1"),sQuery(id+"F0.wireOp",EDGE,"E2"),sQuery(id+"F0.wireOp",EDGE,"E3"),sQuery(id+"F0.wireOp",EDGE,"E4"),sQuery(id+"F0.wireOp",EDGE,"E5"),sQuery(id+"F0.wireOp",EDGE,"E6"),sQuery(id+"F0.wireOp",EDGE,"E7"),sQuery(id+"F0.wireOp",EDGE,"E8"),sQuery(id+"F0.wireOp",EDGE,"E9"),sQuery(id+"F0.wireOp",EDGE,"E16"),sQuery(id+"F0.wireOp",EDGE,"E18"),sQuery(id+"F0.wireOp",EDGE,"E22"),sQuery(id+"F0.wireOp",EDGE,"E23"),sQuery(id+"F0.wireOp",EDGE,"E28"),sQuery(id+"F0.wireOp",EDGE,"E29"),sQuery(id+"F0.wireOp",EDGE,"E30"),sQuery(id+"F0.wireOp",EDGE,"E32"),sQuery(id+"F0.wireOp",EDGE,"E38"),sQuery(id+"F0.wireOp",EDGE,"E39"),sQuery(id+"F0.wireOp",EDGE,"E40"),sQuery(id+"F0.wireOp",EDGE,"E42"),sQuery(id+"F0.wireOp",EDGE,"E48"),sQuery(id+"F0.wireOp",EDGE,"E49"),sQuery(id+"F0.wireOp",EDGE,"E50"),sQuery(id+"F0.wireOp",EDGE,"E52"),sQuery(id+"F0.wireOp",EDGE,"E58"),sQuery(id+"F0.wireOp",EDGE,"E59"),sQuery(id+"F0.wireOp",EDGE,"E60"),sQuery(id+"F0.wireOp",EDGE,"E62")])],"isStart":false}),makeQuery(id+"F3.opExtrude","SWEPT_FACE",FACE,{"disambiguationData":[OSD([sQuery(id+"F1.wireOp",EDGE,"E91"),sQuery(id+"F1.wireOp",EDGE,"E92"),sQuery(id+"F1.wireOp",EDGE,"E98")])]})]});
            var Q71;
            Q71=makeQuery(id+"F2.opExtrude","CAP_EDGE",EDGE,{"disambiguationData":[OSD([sQuery(id+"F0.wireOp",EDGE,"E48")])],"isStart":false});
            var Q72;
            Q72=makeQuery(id+"F2.opExtrude","CAP_EDGE",EDGE,{"disambiguationData":[OSD([sQuery(id+"F0.wireOp",EDGE,"E58")])],"isStart":false});
            var Q73;
            {var subQ0=sQuery(id+"F0.wireOp",EDGE,"E3");Q73=makeQuery(id+"F3.boolean.opBoolean","SPLIT",EDGE,{"disambiguationData":[TD([makeQuery(id+"F2.opExtrude","CAP_FACE",FACE,{"disambiguationData":[OSD([sQuery(id+"F0.wireOp",EDGE,"E1"),sQuery(id+"F0.wireOp",EDGE,"E2"),subQ0,sQuery(id+"F0.wireOp",EDGE,"E4"),sQuery(id+"F0.wireOp",EDGE,"E5"),sQuery(id+"F0.wireOp",EDGE,"E6"),sQuery(id+"F0.wireOp",EDGE,"E7"),sQuery(id+"F0.wireOp",EDGE,"E8"),sQuery(id+"F0.wireOp",EDGE,"E9"),sQuery(id+"F0.wireOp",EDGE,"E16"),sQuery(id+"F0.wireOp",EDGE,"E18"),sQuery(id+"F0.wireOp",EDGE,"E22"),sQuery(id+"F0.wireOp",EDGE,"E23"),sQuery(id+"F0.wireOp",EDGE,"E28"),sQuery(id+"F0.wireOp",EDGE,"E29"),sQuery(id+"F0.wireOp",EDGE,"E30"),sQuery(id+"F0.wireOp",EDGE,"E32"),sQuery(id+"F0.wireOp",EDGE,"E38"),sQuery(id+"F0.wireOp",EDGE,"E39"),sQuery(id+"F0.wireOp",EDGE,"E40"),sQuery(id+"F0.wireOp",EDGE,"E42"),sQuery(id+"F0.wireOp",EDGE,"E48"),sQuery(id+"F0.wireOp",EDGE,"E49"),sQuery(id+"F0.wireOp",EDGE,"E50"),sQuery(id+"F0.wireOp",EDGE,"E52"),sQuery(id+"F0.wireOp",EDGE,"E58"),sQuery(id+"F0.wireOp",EDGE,"E59"),sQuery(id+"F0.wireOp",EDGE,"E60"),sQuery(id+"F0.wireOp",EDGE,"E62")])],"isStart":true}),makeQuery(id+"F2.opExtrude","SWEPT_FACE",FACE,{"disambiguationData":[OSD([subQ0])]}),makeQuery(id+"F3.opExtrude","SWEPT_FACE",FACE,{"disambiguationData":[OSD([sQuery(id+"F1.wireOp",EDGE,"E69"),sQuery(id+"F1.wireOp",EDGE,"E70"),sQuery(id+"F1.wireOp",EDGE,"E76")])]}),makeQuery(id+"F3.opExtrude","SWEPT_FACE",FACE,{"disambiguationData":[OSD([sQuery(id+"F1.wireOp",EDGE,"E80"),sQuery(id+"F1.wireOp",EDGE,"E81"),sQuery(id+"F1.wireOp",EDGE,"E87")])]})])],"derivedFrom":makeQuery(id+"F2.opExtrude","CAP_EDGE",EDGE,{"disambiguationData":[OSD([subQ0])],"isStart":true})});}
            var Q74;
            Q74=makeQuery(id+"F2.opExtrude","SWEPT_EDGE",EDGE,{"disambiguationData":[OSD([sQuery(id+"F0.wireOp",EDGE,"E48"),sQuery(id+"F0.wireOp",EDGE,"E52")])]});
            var Q75;
            Q75=makeQuery(id+"F2.opExtrude","CAP_EDGE",EDGE,{"disambiguationData":[OSD([sQuery(id+"F0.wireOp",EDGE,"E28")])],"isStart":true});
            var Q76;
            Q76=makeQuery(id+"F2.opExtrude","CAP_EDGE",EDGE,{"disambiguationData":[OSD([sQuery(id+"F0.wireOp",EDGE,"E48")])],"isStart":true});
            var Q77;
            Q77=makeQuery(id+"F2.opExtrude","CAP_EDGE",EDGE,{"disambiguationData":[OSD([sQuery(id+"F0.wireOp",EDGE,"E62")])],"isStart":false});
            var Q78;
            Q78=makeQuery(id+"F3.boolean.opBoolean","COPY",EDGE,{"disambiguationData":[OD(1.0)],"derivedFrom":makeQuery(id+"F3.opExtrude","CAP_EDGE",EDGE,{"disambiguationData":[OSD([sQuery(id+"F1.wireOp",EDGE,"E69"),sQuery(id+"F1.wireOp",EDGE,"E70"),sQuery(id+"F1.wireOp",EDGE,"E76")])],"isStart":true})});
            var Q79;
            Q79=makeQuery(id+"F3.boolean.opBoolean","INTERSECT",EDGE,{"disambiguationData":[OD(1.0)],"derivedFrom":[makeQuery(id+"F2.opExtrude","SWEPT_FACE",FACE,{"disambiguationData":[OSD([sQuery(id+"F0.wireOp",EDGE,"E3")])]}),makeQuery(id+"F3.opExtrude","SWEPT_FACE",FACE,{"disambiguationData":[OSD([sQuery(id+"F1.wireOp",EDGE,"E91"),sQuery(id+"F1.wireOp",EDGE,"E92"),sQuery(id+"F1.wireOp",EDGE,"E98")])]})]});
            var Q80;
            Q80=makeQuery(id+"F2.opExtrude","SWEPT_EDGE",EDGE,{"disambiguationData":[OSD([sQuery(id+"F0.wireOp",EDGE,"E48"),sQuery(id+"F0.wireOp",EDGE,"E50")])]});
            var Q81;
            Q81=makeQuery(id+"F2.opExtrude","CAP_EDGE",EDGE,{"disambiguationData":[OSD([sQuery(id+"F0.wireOp",EDGE,"E16")])],"isStart":true});
            var Q82;
            Q82=makeQuery(id+"F2.opExtrude","CAP_EDGE",EDGE,{"disambiguationData":[OSD([sQuery(id+"F0.wireOp",EDGE,"E58")])],"isStart":true});
            var Q83;
            Q83=makeQuery(id+"F2.opExtrude","CAP_EDGE",EDGE,{"disambiguationData":[OSD([sQuery(id+"F0.wireOp",EDGE,"E38")])],"isStart":true});
            var Q84;
            Q84=makeQuery(id+"F2.opExtrude","CAP_EDGE",EDGE,{"disambiguationData":[OSD([sQuery(id+"F0.wireOp",EDGE,"E23")])],"isStart":true});
            var Q85;
            Q85=makeQuery(id+"F2.opExtrude","CAP_EDGE",EDGE,{"disambiguationData":[OSD([sQuery(id+"F0.wireOp",EDGE,"E52")])],"isStart":false});
            var Q86;
            Q86=makeQuery(id+"F2.opExtrude","SWEPT_EDGE",EDGE,{"disambiguationData":[OSD([sQuery(id+"F0.wireOp",EDGE,"E59"),sQuery(id+"F0.wireOp",EDGE,"E62")])]});
            var Q87;
            Q87=makeQuery(id+"F2.opExtrude","CAP_EDGE",EDGE,{"disambiguationData":[OSD([sQuery(id+"F0.wireOp",EDGE,"E32")])],"isStart":true});
            var Q88;
            Q88=makeQuery(id+"F2.opExtrude","CAP_EDGE",EDGE,{"disambiguationData":[OSD([sQuery(id+"F0.wireOp",EDGE,"E60")])],"isStart":false});
            var Q89;
            Q89=makeQuery(id+"F2.opExtrude","SWEPT_EDGE",EDGE,{"disambiguationData":[OSD([sQuery(id+"F0.wireOp",EDGE,"E58"),sQuery(id+"F0.wireOp",EDGE,"E62")])]});
            var Q90;
            Q90=makeQuery(id+"F2.opExtrude","CAP_EDGE",EDGE,{"disambiguationData":[OSD([sQuery(id+"F0.wireOp",EDGE,"E30")])],"isStart":true});
            var Q91;
            Q91=makeQuery(id+"F3.boolean.opBoolean","COPY",EDGE,{"disambiguationData":[OD(1.0)],"derivedFrom":makeQuery(id+"F3.opExtrude","CAP_EDGE",EDGE,{"disambiguationData":[OSD([sQuery(id+"F1.wireOp",EDGE,"E91"),sQuery(id+"F1.wireOp",EDGE,"E92"),sQuery(id+"F1.wireOp",EDGE,"E98")])],"isStart":true})});
            var Q92;
            Q92=makeQuery(id+"F2.opExtrude","SWEPT_EDGE",EDGE,{"disambiguationData":[OSD([sQuery(id+"F0.wireOp",EDGE,"E58"),sQuery(id+"F0.wireOp",EDGE,"E60")])]});
            var Q93;
            Q93=makeQuery(id+"F3.boolean.opBoolean","INTERSECT",EDGE,{"derivedFrom":[makeQuery(id+"F2.opExtrude","CAP_FACE",FACE,{"disambiguationData":[OSD([sQuery(id+"F0.wireOp",EDGE,"E1"),sQuery(id+"F0.wireOp",EDGE,"E2"),sQuery(id+"F0.wireOp",EDGE,"E3"),sQuery(id+"F0.wireOp",EDGE,"E4"),sQuery(id+"F0.wireOp",EDGE,"E5"),sQuery(id+"F0.wireOp",EDGE,"E6"),sQuery(id+"F0.wireOp",EDGE,"E7"),sQuery(id+"F0.wireOp",EDGE,"E8"),sQuery(id+"F0.wireOp",EDGE,"E9"),sQuery(id+"F0.wireOp",EDGE,"E16"),sQuery(id+"F0.wireOp",EDGE,"E18"),sQuery(id+"F0.wireOp",EDGE,"E22"),sQuery(id+"F0.wireOp",EDGE,"E23"),sQuery(id+"F0.wireOp",EDGE,"E28"),sQuery(id+"F0.wireOp",EDGE,"E29"),sQuery(id+"F0.wireOp",EDGE,"E30"),sQuery(id+"F0.wireOp",EDGE,"E32"),sQuery(id+"F0.wireOp",EDGE,"E38"),sQuery(id+"F0.wireOp",EDGE,"E39"),sQuery(id+"F0.wireOp",EDGE,"E40"),sQuery(id+"F0.wireOp",EDGE,"E42"),sQuery(id+"F0.wireOp",EDGE,"E48"),sQuery(id+"F0.wireOp",EDGE,"E49"),sQuery(id+"F0.wireOp",EDGE,"E50"),sQuery(id+"F0.wireOp",EDGE,"E52"),sQuery(id+"F0.wireOp",EDGE,"E58"),sQuery(id+"F0.wireOp",EDGE,"E59"),sQuery(id+"F0.wireOp",EDGE,"E60"),sQuery(id+"F0.wireOp",EDGE,"E62")])],"isStart":false}),makeQuery(id+"F3.opExtrude","SWEPT_FACE",FACE,{"disambiguationData":[OSD([sQuery(id+"F1.wireOp",EDGE,"E95")])]})]});
            var Q94;
            Q94=makeQuery(id+"F3.boolean.opBoolean","COPY",EDGE,{"disambiguationData":[OD(0.0)],"derivedFrom":makeQuery(id+"F3.opExtrude","CAP_EDGE",EDGE,{"disambiguationData":[OSD([sQuery(id+"F1.wireOp",EDGE,"E91"),sQuery(id+"F1.wireOp",EDGE,"E92"),sQuery(id+"F1.wireOp",EDGE,"E98")])],"isStart":true})});
            var Q95;
            Q95=makeQuery(id+"F3.boolean.opBoolean","INTERSECT",EDGE,{"disambiguationData":[OD(0.0)],"derivedFrom":[makeQuery(id+"F2.opExtrude","SWEPT_FACE",FACE,{"disambiguationData":[OSD([sQuery(id+"F0.wireOp",EDGE,"E3")])]}),makeQuery(id+"F3.opExtrude","SWEPT_FACE",FACE,{"disambiguationData":[OSD([sQuery(id+"F1.wireOp",EDGE,"E91"),sQuery(id+"F1.wireOp",EDGE,"E92"),sQuery(id+"F1.wireOp",EDGE,"E98")])]})]});
            var Q96;
            Q96=makeQuery(id+"F3.boolean.opBoolean","COPY",EDGE,{"derivedFrom":makeQuery(id+"F3.opExtrude","CAP_EDGE",EDGE,{"disambiguationData":[OSD([sQuery(id+"F1.wireOp",EDGE,"E95")])],"isStart":true})});
            var Q97;
            Q97=makeQuery(id+"F3.boolean.opBoolean","COPY",EDGE,{"derivedFrom":makeQuery(id+"F3.opExtrude","SWEPT_EDGE",EDGE,{"disambiguationData":[OSD([sQuery(id+"F1.wireOp",EDGE,"E92"),sQuery(id+"F1.wireOp",EDGE,"E95")])]})});
            var Q98;
            Q98=makeQuery(id+"F3.boolean.opBoolean","COPY",EDGE,{"derivedFrom":makeQuery(id+"F3.opExtrude","SWEPT_EDGE",EDGE,{"disambiguationData":[OSD([sQuery(id+"F1.wireOp",EDGE,"E91"),sQuery(id+"F1.wireOp",EDGE,"E95")])]})});
            var Q99;
            Q99=makeQuery(id+"F2.opExtrude","CAP_EDGE",EDGE,{"disambiguationData":[OSD([sQuery(id+"F0.wireOp",EDGE,"E49")])],"isStart":true});
            var Q100;
            {var subQ0=sQuery(id+"F0.wireOp",EDGE,"E3");var subQ1=sQuery(id+"F0.wireOp",EDGE,"E2");Q100=makeQuery(id+"F3.boolean.opBoolean","SPLIT",EDGE,{"disambiguationData":[TD([makeQuery(id+"F2.opExtrude","CAP_FACE",FACE,{"disambiguationData":[OSD([sQuery(id+"F0.wireOp",EDGE,"E1"),subQ1,subQ0,sQuery(id+"F0.wireOp",EDGE,"E4"),sQuery(id+"F0.wireOp",EDGE,"E5"),sQuery(id+"F0.wireOp",EDGE,"E6"),sQuery(id+"F0.wireOp",EDGE,"E7"),sQuery(id+"F0.wireOp",EDGE,"E8"),sQuery(id+"F0.wireOp",EDGE,"E9"),sQuery(id+"F0.wireOp",EDGE,"E16"),sQuery(id+"F0.wireOp",EDGE,"E18"),sQuery(id+"F0.wireOp",EDGE,"E22"),sQuery(id+"F0.wireOp",EDGE,"E23"),sQuery(id+"F0.wireOp",EDGE,"E28"),sQuery(id+"F0.wireOp",EDGE,"E29"),sQuery(id+"F0.wireOp",EDGE,"E30"),sQuery(id+"F0.wireOp",EDGE,"E32"),sQuery(id+"F0.wireOp",EDGE,"E38"),sQuery(id+"F0.wireOp",EDGE,"E39"),sQuery(id+"F0.wireOp",EDGE,"E40"),sQuery(id+"F0.wireOp",EDGE,"E42"),sQuery(id+"F0.wireOp",EDGE,"E48"),sQuery(id+"F0.wireOp",EDGE,"E49"),sQuery(id+"F0.wireOp",EDGE,"E50"),sQuery(id+"F0.wireOp",EDGE,"E52"),sQuery(id+"F0.wireOp",EDGE,"E58"),sQuery(id+"F0.wireOp",EDGE,"E59"),sQuery(id+"F0.wireOp",EDGE,"E60"),sQuery(id+"F0.wireOp",EDGE,"E62")])],"isStart":true}),makeQuery(id+"F2.opExtrude","SWEPT_FACE",FACE,{"disambiguationData":[OSD([subQ1])]}),makeQuery(id+"F2.opExtrude","SWEPT_FACE",FACE,{"disambiguationData":[OSD([subQ0])]}),makeQuery(id+"F3.opExtrude","SWEPT_FACE",FACE,{"disambiguationData":[OSD([sQuery(id+"F1.wireOp",EDGE,"E91"),sQuery(id+"F1.wireOp",EDGE,"E92"),sQuery(id+"F1.wireOp",EDGE,"E98")])]})])],"derivedFrom":makeQuery(id+"F2.opExtrude","CAP_EDGE",EDGE,{"disambiguationData":[OSD([subQ0])],"isStart":true})});}
            var Q101;
            Q101=makeQuery(id+"F2.opExtrude","CAP_EDGE",EDGE,{"disambiguationData":[OSD([sQuery(id+"F0.wireOp",EDGE,"E59")])],"isStart":true});
            var Q102;
            Q102=makeQuery(id+"F2.opExtrude","SWEPT_EDGE",EDGE,{"disambiguationData":[OSD([sQuery(id+"F0.wireOp",EDGE,"E49"),sQuery(id+"F0.wireOp",EDGE,"E52")])]});
            var Q103;
            Q103=makeQuery(id+"F2.opExtrude","SWEPT_EDGE",EDGE,{"disambiguationData":[OSD([sQuery(id+"F0.wireOp",EDGE,"E59"),sQuery(id+"F0.wireOp",EDGE,"E60")])]});
            var Q104;
            Q104=makeQuery(id+"F2.opExtrude","CAP_EDGE",EDGE,{"disambiguationData":[OSD([sQuery(id+"F0.wireOp",EDGE,"E42")])],"isStart":true});
            var Q105;
            Q105=makeQuery(id+"F2.opExtrude","CAP_EDGE",EDGE,{"disambiguationData":[OSD([sQuery(id+"F0.wireOp",EDGE,"E62")])],"isStart":true});
            var Q106;
            Q106=makeQuery(id+"F2.opExtrude","CAP_EDGE",EDGE,{"disambiguationData":[OSD([sQuery(id+"F0.wireOp",EDGE,"E52")])],"isStart":true});
            var Q107;
            Q107=makeQuery(id+"F2.opExtrude","CAP_EDGE",EDGE,{"disambiguationData":[OSD([sQuery(id+"F0.wireOp",EDGE,"E50")])],"isStart":true});
            fillet(context, id + "F4", {"entities" : qUnion([Q0, Q1, Q2, Q3, Q4, Q5, Q6, Q7, Q8, Q9, Q10, Q11, Q12, Q13, Q14, Q15, Q16, Q17, Q18, Q19, Q20, Q21, Q22, Q23, Q24, Q25, Q26, Q27, Q28, Q29, Q30, Q31, Q32, Q33, Q34, Q35, Q36, Q37, Q38, Q39, Q40, Q41, Q42, Q43, Q44, Q45, Q46, Q47, Q48, Q49, Q50, Q51, Q52, Q53, Q54, Q55, Q56, Q57, Q58, Q59, Q60, Q61, Q62, Q63, Q64, Q65, Q66, Q67, Q68, Q69, Q70, Q71, Q72, Q73, Q74, Q75, Q76, Q77, Q78, Q79, Q80, Q81, Q82, Q83, Q84, Q85, Q86, Q87, Q88, Q89, Q90, Q91, Q92, Q93, Q94, Q95, Q96, Q97, Q98, Q99, Q100, Q101, Q102, Q103, Q104, Q105, Q106, Q107]), "radius" : 1 * mm, "tangentPropagation" : true, "allowEdgeOverflow" : false});
        }
        {
            var Q0;
            Q0=qCreatedBy(makeId("Front.planeOp"),FACE);
            var sketch = newSketch(context, id + "F5", { "sketchPlane" : qUnion([Q0])});
            skArc(sketch, "E99", {"start": v(-45.2, 405.67) * mm, "mid": v(-35, 401.67) * mm, "end": v(-24.8, 405.67) * mm});
            skLineSegment(sketch, "E100", {"start": v(-24.8, 427.67) * mm, "end": v(-24.8, 405.67) * mm});
            skLineSegment(sketch, "E101", {"start": v(-45.2, 405.67) * mm, "end": v(-45.2, 427.67) * mm});
            skArc(sketch, "E102.trimOffspring", {"start": v(-24.8, 427.67) * mm, "mid": v(-35, 431.67) * mm, "end": v(-45.2, 427.67) * mm});
            skSolve(sketch);
        }
        {
            var Q0;
            Q0 = qSketchRegion(id + "F5", true);
            extrude(context, id + "F6", {"entities" : qUnion([Q0]), "endBound" : BoundingType.SYMMETRIC, "depth" : 600 * mm});
        }
        {
            var Q0;
            Q0=qCreatedBy(makeId("Right.planeOp"),FACE);
            var sketch = newSketch(context, id + "F7", { "sketchPlane" : qUnion([Q0])});
            skLineSegment(sketch, "E103.bottom", {"start": v(0, 427.67) * mm, "end": v(-10, 427.67) * mm});
            skLineSegment(sketch, "E103.top", {"start": v(0, 437.67) * mm, "end": v(-10, 437.67) * mm});
            skLineSegment(sketch, "E103.left", {"start": v(0, 427.67) * mm, "end": v(0, 437.67) * mm});
            skLineSegment(sketch, "E103.right", {"start": v(-10, 427.67) * mm, "end": v(-10, 437.67) * mm});
            skLineSegment(sketch, "E104.bottom", {"start": v(0, 395.67) * mm, "end": v(-10, 395.67) * mm});
            skLineSegment(sketch, "E104.left", {"start": v(0, 395.67) * mm, "end": v(0, 405.67) * mm});
            skLineSegment(sketch, "E104.top", {"start": v(0, 405.67) * mm, "end": v(-10, 405.67) * mm});
            skLineSegment(sketch, "E104.right", {"start": v(-10, 395.67) * mm, "end": v(-10, 405.67) * mm});
            skLineSegment(sketch, "E105.1.0.0", {"start": v(110, 395.67) * mm, "end": v(110, 405.67) * mm});
            skLineSegment(sketch, "E105.1.0.1", {"start": v(110, 427.67) * mm, "end": v(110, 437.67) * mm});
            skLineSegment(sketch, "E105.1.0.2", {"start": v(120, 405.67) * mm, "end": v(110, 405.67) * mm});
            skLineSegment(sketch, "E105.1.0.3", {"start": v(120, 395.67) * mm, "end": v(120, 405.67) * mm});
            skLineSegment(sketch, "E105.1.0.4", {"start": v(120, 395.67) * mm, "end": v(110, 395.67) * mm});
            skLineSegment(sketch, "E105.1.0.5", {"start": v(120, 427.67) * mm, "end": v(120, 437.67) * mm});
            skLineSegment(sketch, "E105.1.0.6", {"start": v(120, 437.67) * mm, "end": v(110, 437.67) * mm});
            skLineSegment(sketch, "E105.1.0.7", {"start": v(120, 427.67) * mm, "end": v(110, 427.67) * mm});
            skLineSegment(sketch, "E105.2.0.0", {"start": v(230, 395.67) * mm, "end": v(230, 405.67) * mm});
            skLineSegment(sketch, "E105.2.0.1", {"start": v(230, 427.67) * mm, "end": v(230, 437.67) * mm});
            skLineSegment(sketch, "E105.2.0.2", {"start": v(240, 405.67) * mm, "end": v(230, 405.67) * mm});
            skLineSegment(sketch, "E105.2.0.3", {"start": v(240, 395.67) * mm, "end": v(240, 405.67) * mm});
            skLineSegment(sketch, "E105.2.0.4", {"start": v(240, 395.67) * mm, "end": v(230, 395.67) * mm});
            skLineSegment(sketch, "E105.2.0.5", {"start": v(240, 427.67) * mm, "end": v(240, 437.67) * mm});
            skLineSegment(sketch, "E105.2.0.6", {"start": v(240, 437.67) * mm, "end": v(230, 437.67) * mm});
            skLineSegment(sketch, "E105.2.0.7", {"start": v(240, 427.67) * mm, "end": v(230, 427.67) * mm});
            skLineSegment(sketch, "E105.direction1", {"start": v(-10, 395.67) * mm, "end": v(110, 395.67) * mm, "construction": true});
            skLineSegment(sketch, "E106.1.0.0", {"start": v(-130, 427.67) * mm, "end": v(-130, 437.67) * mm});
            skLineSegment(sketch, "E106.1.0.1", {"start": v(-120, 437.67) * mm, "end": v(-130, 437.67) * mm});
            skLineSegment(sketch, "E106.1.0.2", {"start": v(-120, 427.67) * mm, "end": v(-130, 427.67) * mm});
            skLineSegment(sketch, "E106.1.0.3", {"start": v(-120, 427.67) * mm, "end": v(-120, 437.67) * mm});
            skLineSegment(sketch, "E106.1.0.4", {"start": v(-120, 405.67) * mm, "end": v(-130, 405.67) * mm});
            skLineSegment(sketch, "E106.1.0.5", {"start": v(-120, 395.67) * mm, "end": v(-120, 405.67) * mm});
            skLineSegment(sketch, "E106.1.0.6", {"start": v(-120, 395.67) * mm, "end": v(-130, 395.67) * mm});
            skLineSegment(sketch, "E106.1.0.7", {"start": v(-130, 395.67) * mm, "end": v(-130, 405.67) * mm});
            skLineSegment(sketch, "E106.2.0.0", {"start": v(-250, 427.67) * mm, "end": v(-250, 437.67) * mm});
            skLineSegment(sketch, "E106.2.0.1", {"start": v(-240, 437.67) * mm, "end": v(-250, 437.67) * mm});
            skLineSegment(sketch, "E106.2.0.2", {"start": v(-240, 427.67) * mm, "end": v(-250, 427.67) * mm});
            skLineSegment(sketch, "E106.2.0.3", {"start": v(-240, 427.67) * mm, "end": v(-240, 437.67) * mm});
            skLineSegment(sketch, "E106.2.0.4", {"start": v(-240, 405.67) * mm, "end": v(-250, 405.67) * mm});
            skLineSegment(sketch, "E106.2.0.5", {"start": v(-240, 395.67) * mm, "end": v(-240, 405.67) * mm});
            skLineSegment(sketch, "E106.2.0.6", {"start": v(-240, 395.67) * mm, "end": v(-250, 395.67) * mm});
            skLineSegment(sketch, "E106.2.0.7", {"start": v(-250, 395.67) * mm, "end": v(-250, 405.67) * mm});
            skLineSegment(sketch, "E106.direction1", {"start": v(-10, 427.67) * mm, "end": v(-130, 427.67) * mm, "construction": true});
            skSolve(sketch);
        }
        {
            var Q0;
            Q0 = qSketchRegion(id + "F7", true);
            extrude(context, id + "F8", {"entities" : qUnion([Q0]), "operationType" : NewBodyOperationType.REMOVE, "endBound" : BoundingType.THROUGH_ALL, "oppositeDirection" : true, "depth" : 25 * mm});
        }
        {
            var Q0;
            Q0=makeQuery(id+"F8.boolean.opBoolean","INTERSECT",EDGE,{"derivedFrom":[makeQuery(id+"F6.opExtrude","SWEPT_FACE",FACE,{"disambiguationData":[OSD([sQuery(id+"F5.wireOp",EDGE,"E102.trimOffspring")])]}),makeQuery(id+"F8.opExtrude","SWEPT_FACE",FACE,{"disambiguationData":[OSD([sQuery(id+"F7.wireOp",EDGE,"E106.1.0.0")])]})]});
            var Q1;
            {var subQ0=sQuery(id+"F5.wireOp",EDGE,"E102.trimOffspring");var subQ1=makeQuery(id+"F6.opExtrude","SWEPT_FACE",FACE,{"disambiguationData":[OSD([subQ0])]});var subQ2=sQuery(id+"F5.wireOp",EDGE,"E101");var subQ3=makeQuery(id+"F6.opExtrude","SWEPT_FACE",FACE,{"disambiguationData":[OSD([subQ2])]});Q1=makeQuery(id+"F8.boolean.opBoolean","SPLIT",EDGE,{"disambiguationData":[topologyDisambiguationEdgeConnected([subQ3,subQ1]),TD([makeQuery(id+"F8.opExtrude","SWEPT_FACE",FACE,{"disambiguationData":[OSD([sQuery(id+"F7.wireOp",EDGE,"E106.2.0.0")])]})])],"derivedFrom":makeQuery(id+"F6.opExtrude","SWEPT_EDGE",EDGE,{"disambiguationData":[OSD([subQ2,subQ0])]})});}
            var Q2;
            Q2=makeQuery(id+"F8.boolean.opBoolean","COPY",EDGE,{"derivedFrom":makeQuery(id+"F8.opExtrude","SWEPT_EDGE",EDGE,{"disambiguationData":[OSD([sQuery(id+"F7.wireOp",EDGE,"E106.1.0.0"),sQuery(id+"F7.wireOp",EDGE,"E106.1.0.2")])]})});
            var Q3;
            Q3=makeQuery(id+"F8.boolean.opBoolean","INTERSECT",EDGE,{"derivedFrom":[makeQuery(id+"F6.opExtrude","SWEPT_FACE",FACE,{"disambiguationData":[OSD([sQuery(id+"F5.wireOp",EDGE,"E102.trimOffspring")])]}),makeQuery(id+"F8.opExtrude","SWEPT_FACE",FACE,{"disambiguationData":[OSD([sQuery(id+"F7.wireOp",EDGE,"E105.2.0.5")])]})]});
            var Q4;
            Q4=makeQuery(id+"F8.boolean.opBoolean","INTERSECT",EDGE,{"derivedFrom":[makeQuery(id+"F6.opExtrude","SWEPT_FACE",FACE,{"disambiguationData":[OSD([sQuery(id+"F5.wireOp",EDGE,"E102.trimOffspring")])]}),makeQuery(id+"F8.opExtrude","SWEPT_FACE",FACE,{"disambiguationData":[OSD([sQuery(id+"F7.wireOp",EDGE,"E106.1.0.3")])]})]});
            var Q5;
            {var subQ0=sQuery(id+"F5.wireOp",EDGE,"E101");var subQ1=makeQuery(id+"F6.opExtrude","SWEPT_FACE",FACE,{"disambiguationData":[OSD([subQ0])]});var subQ2=sQuery(id+"F5.wireOp",EDGE,"E99");var subQ3=makeQuery(id+"F6.opExtrude","SWEPT_FACE",FACE,{"disambiguationData":[OSD([subQ2])]});Q5=makeQuery(id+"F8.boolean.opBoolean","SPLIT",EDGE,{"disambiguationData":[topologyDisambiguationEdgeConnected([subQ3,subQ1]),TD([makeQuery(id+"F8.opExtrude","SWEPT_FACE",FACE,{"disambiguationData":[OSD([sQuery(id+"F7.wireOp",EDGE,"E106.2.0.7")])]})])],"derivedFrom":makeQuery(id+"F6.opExtrude","SWEPT_EDGE",EDGE,{"disambiguationData":[OSD([subQ2,subQ0])]})});}
            var Q6;
            Q6=makeQuery(id+"F8.boolean.opBoolean","INTERSECT",EDGE,{"derivedFrom":[makeQuery(id+"F6.opExtrude","SWEPT_FACE",FACE,{"disambiguationData":[OSD([sQuery(id+"F5.wireOp",EDGE,"E102.trimOffspring")])]}),makeQuery(id+"F8.opExtrude","SWEPT_FACE",FACE,{"disambiguationData":[OSD([sQuery(id+"F7.wireOp",EDGE,"E105.1.0.5")])]})]});
            var Q7;
            {var subQ0=sQuery(id+"F5.wireOp",EDGE,"E101");var subQ1=makeQuery(id+"F6.opExtrude","SWEPT_FACE",FACE,{"disambiguationData":[OSD([subQ0])]});var subQ2=sQuery(id+"F5.wireOp",EDGE,"E99");var subQ3=makeQuery(id+"F6.opExtrude","SWEPT_FACE",FACE,{"disambiguationData":[OSD([subQ2])]});Q7=makeQuery(id+"F8.boolean.opBoolean","SPLIT",EDGE,{"disambiguationData":[topologyDisambiguationEdgeConnected([subQ3,subQ1]),TD([makeQuery(id+"F8.opExtrude","SWEPT_FACE",FACE,{"disambiguationData":[OSD([sQuery(id+"F7.wireOp",EDGE,"E105.2.0.3")])]})])],"derivedFrom":makeQuery(id+"F6.opExtrude","SWEPT_EDGE",EDGE,{"disambiguationData":[OSD([subQ2,subQ0])]})});}
            var Q8;
            Q8=makeQuery(id+"F8.boolean.opBoolean","COPY",EDGE,{"derivedFrom":makeQuery(id+"F8.opExtrude","SWEPT_EDGE",EDGE,{"disambiguationData":[OSD([sQuery(id+"F7.wireOp",EDGE,"E103.bottom"),sQuery(id+"F7.wireOp",EDGE,"E103.right")])]})});
            var Q9;
            Q9=makeQuery(id+"F8.boolean.opBoolean","COPY",EDGE,{"derivedFrom":makeQuery(id+"F8.opExtrude","SWEPT_EDGE",EDGE,{"disambiguationData":[OSD([sQuery(id+"F7.wireOp",EDGE,"E104.top"),sQuery(id+"F7.wireOp",EDGE,"E104.right")])]})});
            var Q10;
            Q10=makeQuery(id+"F8.boolean.opBoolean","INTERSECT",EDGE,{"derivedFrom":[makeQuery(id+"F6.opExtrude","SWEPT_FACE",FACE,{"disambiguationData":[OSD([sQuery(id+"F5.wireOp",EDGE,"E102.trimOffspring")])]}),makeQuery(id+"F8.opExtrude","SWEPT_FACE",FACE,{"disambiguationData":[OSD([sQuery(id+"F7.wireOp",EDGE,"E105.2.0.1")])]})]});
            var Q11;
            Q11=makeQuery(id+"F8.boolean.opBoolean","COPY",EDGE,{"derivedFrom":makeQuery(id+"F8.opExtrude","SWEPT_EDGE",EDGE,{"disambiguationData":[OSD([sQuery(id+"F7.wireOp",EDGE,"E105.1.0.1"),sQuery(id+"F7.wireOp",EDGE,"E105.1.0.7")])]})});
            var Q12;
            Q12=makeQuery(id+"F8.boolean.opBoolean","INTERSECT",EDGE,{"derivedFrom":[makeQuery(id+"F6.opExtrude","SWEPT_FACE",FACE,{"disambiguationData":[OSD([sQuery(id+"F5.wireOp",EDGE,"E102.trimOffspring")])]}),makeQuery(id+"F8.opExtrude","SWEPT_FACE",FACE,{"disambiguationData":[OSD([sQuery(id+"F7.wireOp",EDGE,"E105.1.0.1")])]})]});
            var Q13;
            Q13=makeQuery(id+"F8.boolean.opBoolean","COPY",EDGE,{"derivedFrom":makeQuery(id+"F8.opExtrude","SWEPT_EDGE",EDGE,{"disambiguationData":[OSD([sQuery(id+"F7.wireOp",EDGE,"E105.2.0.0"),sQuery(id+"F7.wireOp",EDGE,"E105.2.0.2")])]})});
            var Q14;
            Q14=makeQuery(id+"F6.opExtrude","CAP_EDGE",EDGE,{"disambiguationData":[OSD([sQuery(id+"F5.wireOp",EDGE,"E102.trimOffspring")])],"isStart":false});
            var Q15;
            Q15=makeQuery(id+"F6.opExtrude","CAP_EDGE",EDGE,{"disambiguationData":[OSD([sQuery(id+"F5.wireOp",EDGE,"E102.trimOffspring")])],"isStart":true});
            var Q16;
            Q16=makeQuery(id+"F6.opExtrude","CAP_EDGE",EDGE,{"disambiguationData":[OSD([sQuery(id+"F5.wireOp",EDGE,"E99")])],"isStart":false});
            var Q17;
            {var subQ0=sQuery(id+"F5.wireOp",EDGE,"E101");var subQ1=makeQuery(id+"F6.opExtrude","SWEPT_FACE",FACE,{"disambiguationData":[OSD([subQ0])]});var subQ2=sQuery(id+"F5.wireOp",EDGE,"E99");var subQ3=makeQuery(id+"F6.opExtrude","SWEPT_FACE",FACE,{"disambiguationData":[OSD([subQ2])]});Q17=makeQuery(id+"F8.boolean.opBoolean","SPLIT",EDGE,{"disambiguationData":[topologyDisambiguationEdgeConnected([subQ3,subQ1]),TD([makeQuery(id+"F8.opExtrude","SWEPT_FACE",FACE,{"disambiguationData":[OSD([sQuery(id+"F7.wireOp",EDGE,"E106.1.0.7")])]})])],"derivedFrom":makeQuery(id+"F6.opExtrude","SWEPT_EDGE",EDGE,{"disambiguationData":[OSD([subQ2,subQ0])]})});}
            var Q18;
            {var subQ0=sQuery(id+"F5.wireOp",EDGE,"E101");var subQ1=makeQuery(id+"F6.opExtrude","SWEPT_FACE",FACE,{"disambiguationData":[OSD([subQ0])]});var subQ2=sQuery(id+"F5.wireOp",EDGE,"E99");var subQ3=makeQuery(id+"F6.opExtrude","SWEPT_FACE",FACE,{"disambiguationData":[OSD([subQ2])]});Q18=makeQuery(id+"F8.boolean.opBoolean","SPLIT",EDGE,{"disambiguationData":[topologyDisambiguationEdgeConnected([subQ3,subQ1]),TD([makeQuery(id+"F8.opExtrude","SWEPT_FACE",FACE,{"disambiguationData":[OSD([sQuery(id+"F7.wireOp",EDGE,"E105.1.0.3")])]})])],"derivedFrom":makeQuery(id+"F6.opExtrude","SWEPT_EDGE",EDGE,{"disambiguationData":[OSD([subQ2,subQ0])]})});}
            var Q19;
            {var subQ0=sQuery(id+"F5.wireOp",EDGE,"E99");var subQ1=makeQuery(id+"F6.opExtrude","SWEPT_FACE",FACE,{"disambiguationData":[OSD([subQ0])]});var subQ2=sQuery(id+"F5.wireOp",EDGE,"E101");var subQ3=makeQuery(id+"F6.opExtrude","SWEPT_FACE",FACE,{"disambiguationData":[OSD([subQ2])]});Q19=makeQuery(id+"F8.boolean.opBoolean","SPLIT",EDGE,{"disambiguationData":[topologyDisambiguationEdgeConnected([subQ1,subQ3]),TD([makeQuery(id+"F8.opExtrude","SWEPT_FACE",FACE,{"disambiguationData":[OSD([sQuery(id+"F7.wireOp",EDGE,"E104.right")])]})])],"derivedFrom":makeQuery(id+"F6.opExtrude","SWEPT_EDGE",EDGE,{"disambiguationData":[OSD([subQ0,subQ2])]})});}
            var Q20;
            Q20=makeQuery(id+"F8.boolean.opBoolean","INTERSECT",EDGE,{"derivedFrom":[makeQuery(id+"F6.opExtrude","SWEPT_FACE",FACE,{"disambiguationData":[OSD([sQuery(id+"F5.wireOp",EDGE,"E102.trimOffspring")])]}),makeQuery(id+"F8.opExtrude","SWEPT_FACE",FACE,{"disambiguationData":[OSD([sQuery(id+"F7.wireOp",EDGE,"E103.right")])]})]});
            var Q21;
            Q21=makeQuery(id+"F8.boolean.opBoolean","INTERSECT",EDGE,{"derivedFrom":[makeQuery(id+"F6.opExtrude","SWEPT_FACE",FACE,{"disambiguationData":[OSD([sQuery(id+"F5.wireOp",EDGE,"E102.trimOffspring")])]}),makeQuery(id+"F8.opExtrude","SWEPT_FACE",FACE,{"disambiguationData":[OSD([sQuery(id+"F7.wireOp",EDGE,"E106.2.0.3")])]})]});
            var Q22;
            {var subQ0=sQuery(id+"F5.wireOp",EDGE,"E99");var subQ1=makeQuery(id+"F6.opExtrude","SWEPT_FACE",FACE,{"disambiguationData":[OSD([subQ0])]});var subQ2=sQuery(id+"F5.wireOp",EDGE,"E101");var subQ3=makeQuery(id+"F6.opExtrude","SWEPT_FACE",FACE,{"disambiguationData":[OSD([subQ2])]});Q22=makeQuery(id+"F8.boolean.opBoolean","SPLIT",EDGE,{"disambiguationData":[topologyDisambiguationEdgeConnected([subQ1,subQ3]),TD([makeQuery(id+"F8.opExtrude","SWEPT_FACE",FACE,{"disambiguationData":[OSD([sQuery(id+"F7.wireOp",EDGE,"E104.left")])]})])],"derivedFrom":makeQuery(id+"F6.opExtrude","SWEPT_EDGE",EDGE,{"disambiguationData":[OSD([subQ0,subQ2])]})});}
            var Q23;
            Q23=makeQuery(id+"F8.boolean.opBoolean","INTERSECT",EDGE,{"derivedFrom":[makeQuery(id+"F6.opExtrude","SWEPT_FACE",FACE,{"disambiguationData":[OSD([sQuery(id+"F5.wireOp",EDGE,"E102.trimOffspring")])]}),makeQuery(id+"F8.opExtrude","SWEPT_FACE",FACE,{"disambiguationData":[OSD([sQuery(id+"F7.wireOp",EDGE,"E103.left")])]})]});
            var Q24;
            Q24=makeQuery(id+"F8.boolean.opBoolean","INTERSECT",EDGE,{"derivedFrom":[makeQuery(id+"F6.opExtrude","SWEPT_FACE",FACE,{"disambiguationData":[OSD([sQuery(id+"F5.wireOp",EDGE,"E102.trimOffspring")])]}),makeQuery(id+"F8.opExtrude","SWEPT_FACE",FACE,{"disambiguationData":[OSD([sQuery(id+"F7.wireOp",EDGE,"E106.2.0.0")])]})]});
            var Q25;
            {var subQ0=sQuery(id+"F5.wireOp",EDGE,"E99");var subQ1=makeQuery(id+"F6.opExtrude","SWEPT_FACE",FACE,{"disambiguationData":[OSD([subQ0])]});var subQ2=sQuery(id+"F5.wireOp",EDGE,"E100");var subQ3=makeQuery(id+"F6.opExtrude","SWEPT_FACE",FACE,{"disambiguationData":[OSD([subQ2])]});Q25=makeQuery(id+"F8.boolean.opBoolean","SPLIT",EDGE,{"disambiguationData":[topologyDisambiguationEdgeConnected([subQ1,subQ3]),TD([makeQuery(id+"F8.opExtrude","SWEPT_FACE",FACE,{"disambiguationData":[OSD([sQuery(id+"F7.wireOp",EDGE,"E104.right")])]})])],"derivedFrom":makeQuery(id+"F6.opExtrude","SWEPT_EDGE",EDGE,{"disambiguationData":[OSD([subQ0,subQ2])]})});}
            var Q26;
            {var subQ0=sQuery(id+"F5.wireOp",EDGE,"E102.trimOffspring");var subQ1=makeQuery(id+"F6.opExtrude","SWEPT_FACE",FACE,{"disambiguationData":[OSD([subQ0])]});var subQ2=sQuery(id+"F5.wireOp",EDGE,"E100");var subQ3=makeQuery(id+"F6.opExtrude","SWEPT_FACE",FACE,{"disambiguationData":[OSD([subQ2])]});Q26=makeQuery(id+"F8.boolean.opBoolean","SPLIT",EDGE,{"disambiguationData":[topologyDisambiguationEdgeConnected([subQ3,subQ1]),TD([makeQuery(id+"F8.opExtrude","SWEPT_FACE",FACE,{"disambiguationData":[OSD([sQuery(id+"F7.wireOp",EDGE,"E106.1.0.0")])]})])],"derivedFrom":makeQuery(id+"F6.opExtrude","SWEPT_EDGE",EDGE,{"disambiguationData":[OSD([subQ2,subQ0])]})});}
            var Q27;
            {var subQ0=sQuery(id+"F5.wireOp",EDGE,"E101");Q27=makeQuery(id+"F8.boolean.opBoolean","SPLIT",EDGE,{"disambiguationData":[topologyDisambiguationEdgeConnected([makeQuery(id+"F6.opExtrude","SWEPT_FACE",FACE,{"disambiguationData":[OSD([subQ0])]}),makeQuery(id+"F8.opExtrude","SWEPT_FACE",FACE,{"disambiguationData":[OSD([sQuery(id+"F7.wireOp",EDGE,"E103.bottom")])]})])],"derivedFrom":makeQuery(id+"F6.opExtrude","SWEPT_EDGE",EDGE,{"disambiguationData":[OSD([subQ0,sQuery(id+"F5.wireOp",EDGE,"E102.trimOffspring")])]})});}
            var Q28;
            {var subQ0=sQuery(id+"F5.wireOp",EDGE,"E100");var subQ1=makeQuery(id+"F6.opExtrude","SWEPT_FACE",FACE,{"disambiguationData":[OSD([subQ0])]});var subQ2=sQuery(id+"F5.wireOp",EDGE,"E99");var subQ3=makeQuery(id+"F6.opExtrude","SWEPT_FACE",FACE,{"disambiguationData":[OSD([subQ2])]});Q28=makeQuery(id+"F8.boolean.opBoolean","SPLIT",EDGE,{"disambiguationData":[topologyDisambiguationEdgeConnected([subQ3,subQ1]),TD([makeQuery(id+"F8.opExtrude","SWEPT_FACE",FACE,{"disambiguationData":[OSD([sQuery(id+"F7.wireOp",EDGE,"E106.2.0.7")])]})])],"derivedFrom":makeQuery(id+"F6.opExtrude","SWEPT_EDGE",EDGE,{"disambiguationData":[OSD([subQ2,subQ0])]})});}
            var Q29;
            {var subQ0=sQuery(id+"F5.wireOp",EDGE,"E100");Q29=makeQuery(id+"F8.boolean.opBoolean","SPLIT",EDGE,{"disambiguationData":[topologyDisambiguationEdgeConnected([makeQuery(id+"F6.opExtrude","SWEPT_FACE",FACE,{"disambiguationData":[OSD([subQ0])]}),makeQuery(id+"F8.opExtrude","SWEPT_FACE",FACE,{"disambiguationData":[OSD([sQuery(id+"F7.wireOp",EDGE,"E105.1.0.7")])]})])],"derivedFrom":makeQuery(id+"F6.opExtrude","SWEPT_EDGE",EDGE,{"disambiguationData":[OSD([subQ0,sQuery(id+"F5.wireOp",EDGE,"E102.trimOffspring")])]})});}
            var Q30;
            Q30=makeQuery(id+"F8.boolean.opBoolean","COPY",EDGE,{"derivedFrom":makeQuery(id+"F8.opExtrude","SWEPT_EDGE",EDGE,{"disambiguationData":[OSD([sQuery(id+"F7.wireOp",EDGE,"E106.2.0.0"),sQuery(id+"F7.wireOp",EDGE,"E106.2.0.2")])]})});
            var Q31;
            {var subQ0=sQuery(id+"F5.wireOp",EDGE,"E100");var subQ1=makeQuery(id+"F6.opExtrude","SWEPT_FACE",FACE,{"disambiguationData":[OSD([subQ0])]});var subQ2=sQuery(id+"F5.wireOp",EDGE,"E99");var subQ3=makeQuery(id+"F6.opExtrude","SWEPT_FACE",FACE,{"disambiguationData":[OSD([subQ2])]});Q31=makeQuery(id+"F8.boolean.opBoolean","SPLIT",EDGE,{"disambiguationData":[topologyDisambiguationEdgeConnected([subQ3,subQ1]),TD([makeQuery(id+"F8.opExtrude","SWEPT_FACE",FACE,{"disambiguationData":[OSD([sQuery(id+"F7.wireOp",EDGE,"E105.1.0.3")])]})])],"derivedFrom":makeQuery(id+"F6.opExtrude","SWEPT_EDGE",EDGE,{"disambiguationData":[OSD([subQ2,subQ0])]})});}
            var Q32;
            {var subQ0=sQuery(id+"F5.wireOp",EDGE,"E101");Q32=makeQuery(id+"F8.boolean.opBoolean","SPLIT",EDGE,{"disambiguationData":[topologyDisambiguationEdgeConnected([makeQuery(id+"F6.opExtrude","SWEPT_FACE",FACE,{"disambiguationData":[OSD([subQ0])]}),makeQuery(id+"F8.opExtrude","SWEPT_FACE",FACE,{"disambiguationData":[OSD([sQuery(id+"F7.wireOp",EDGE,"E106.1.0.2")])]})])],"derivedFrom":makeQuery(id+"F6.opExtrude","SWEPT_EDGE",EDGE,{"disambiguationData":[OSD([subQ0,sQuery(id+"F5.wireOp",EDGE,"E102.trimOffspring")])]})});}
            var Q33;
            Q33=makeQuery(id+"F8.boolean.opBoolean","COPY",EDGE,{"derivedFrom":makeQuery(id+"F8.opExtrude","SWEPT_EDGE",EDGE,{"disambiguationData":[OSD([sQuery(id+"F7.wireOp",EDGE,"E105.2.0.2"),sQuery(id+"F7.wireOp",EDGE,"E105.2.0.3")])]})});
            var Q34;
            {var subQ0=sQuery(id+"F5.wireOp",EDGE,"E102.trimOffspring");var subQ1=makeQuery(id+"F6.opExtrude","SWEPT_FACE",FACE,{"disambiguationData":[OSD([subQ0])]});var subQ2=sQuery(id+"F5.wireOp",EDGE,"E100");var subQ3=makeQuery(id+"F6.opExtrude","SWEPT_FACE",FACE,{"disambiguationData":[OSD([subQ2])]});Q34=makeQuery(id+"F8.boolean.opBoolean","SPLIT",EDGE,{"disambiguationData":[topologyDisambiguationEdgeConnected([subQ3,subQ1]),TD([makeQuery(id+"F8.opExtrude","SWEPT_FACE",FACE,{"disambiguationData":[OSD([sQuery(id+"F7.wireOp",EDGE,"E105.1.0.5")])]})])],"derivedFrom":makeQuery(id+"F6.opExtrude","SWEPT_EDGE",EDGE,{"disambiguationData":[OSD([subQ2,subQ0])]})});}
            var Q35;
            Q35=makeQuery(id+"F8.boolean.opBoolean","COPY",EDGE,{"derivedFrom":makeQuery(id+"F8.opExtrude","SWEPT_EDGE",EDGE,{"disambiguationData":[OSD([sQuery(id+"F7.wireOp",EDGE,"E105.2.0.5"),sQuery(id+"F7.wireOp",EDGE,"E105.2.0.7")])]})});
            var Q36;
            {var subQ0=sQuery(id+"F5.wireOp",EDGE,"E100");var subQ1=makeQuery(id+"F6.opExtrude","SWEPT_FACE",FACE,{"disambiguationData":[OSD([subQ0])]});var subQ2=sQuery(id+"F5.wireOp",EDGE,"E99");var subQ3=makeQuery(id+"F6.opExtrude","SWEPT_FACE",FACE,{"disambiguationData":[OSD([subQ2])]});Q36=makeQuery(id+"F8.boolean.opBoolean","SPLIT",EDGE,{"disambiguationData":[topologyDisambiguationEdgeConnected([subQ3,subQ1]),TD([makeQuery(id+"F8.opExtrude","SWEPT_FACE",FACE,{"disambiguationData":[OSD([sQuery(id+"F7.wireOp",EDGE,"E105.2.0.3")])]})])],"derivedFrom":makeQuery(id+"F6.opExtrude","SWEPT_EDGE",EDGE,{"disambiguationData":[OSD([subQ2,subQ0])]})});}
            var Q37;
            {var subQ0=sQuery(id+"F5.wireOp",EDGE,"E102.trimOffspring");var subQ1=makeQuery(id+"F6.opExtrude","SWEPT_FACE",FACE,{"disambiguationData":[OSD([subQ0])]});var subQ2=sQuery(id+"F5.wireOp",EDGE,"E101");var subQ3=makeQuery(id+"F6.opExtrude","SWEPT_FACE",FACE,{"disambiguationData":[OSD([subQ2])]});Q37=makeQuery(id+"F8.boolean.opBoolean","SPLIT",EDGE,{"disambiguationData":[topologyDisambiguationEdgeConnected([subQ3,subQ1]),TD([makeQuery(id+"F8.opExtrude","SWEPT_FACE",FACE,{"disambiguationData":[OSD([sQuery(id+"F7.wireOp",EDGE,"E105.1.0.5")])]})])],"derivedFrom":makeQuery(id+"F6.opExtrude","SWEPT_EDGE",EDGE,{"disambiguationData":[OSD([subQ2,subQ0])]})});}
            var Q38;
            {var subQ0=sQuery(id+"F5.wireOp",EDGE,"E101");Q38=makeQuery(id+"F8.boolean.opBoolean","SPLIT",EDGE,{"disambiguationData":[topologyDisambiguationEdgeConnected([makeQuery(id+"F6.opExtrude","SWEPT_FACE",FACE,{"disambiguationData":[OSD([subQ0])]}),makeQuery(id+"F8.opExtrude","SWEPT_FACE",FACE,{"disambiguationData":[OSD([sQuery(id+"F7.wireOp",EDGE,"E104.top")])]})])],"derivedFrom":makeQuery(id+"F6.opExtrude","SWEPT_EDGE",EDGE,{"disambiguationData":[OSD([sQuery(id+"F5.wireOp",EDGE,"E99"),subQ0])]})});}
            var Q39;
            {var subQ0=sQuery(id+"F5.wireOp",EDGE,"E101");Q39=makeQuery(id+"F8.boolean.opBoolean","SPLIT",EDGE,{"disambiguationData":[topologyDisambiguationEdgeConnected([makeQuery(id+"F6.opExtrude","SWEPT_FACE",FACE,{"disambiguationData":[OSD([subQ0])]}),makeQuery(id+"F8.opExtrude","SWEPT_FACE",FACE,{"disambiguationData":[OSD([sQuery(id+"F7.wireOp",EDGE,"E105.2.0.7")])]})])],"derivedFrom":makeQuery(id+"F6.opExtrude","SWEPT_EDGE",EDGE,{"disambiguationData":[OSD([subQ0,sQuery(id+"F5.wireOp",EDGE,"E102.trimOffspring")])]})});}
            var Q40;
            Q40=makeQuery(id+"F8.boolean.opBoolean","COPY",EDGE,{"derivedFrom":makeQuery(id+"F8.opExtrude","SWEPT_EDGE",EDGE,{"disambiguationData":[OSD([sQuery(id+"F7.wireOp",EDGE,"E105.2.0.1"),sQuery(id+"F7.wireOp",EDGE,"E105.2.0.7")])]})});
            var Q41;
            {var subQ0=sQuery(id+"F5.wireOp",EDGE,"E102.trimOffspring");var subQ1=makeQuery(id+"F6.opExtrude","SWEPT_FACE",FACE,{"disambiguationData":[OSD([subQ0])]});var subQ2=sQuery(id+"F5.wireOp",EDGE,"E101");var subQ3=makeQuery(id+"F6.opExtrude","SWEPT_FACE",FACE,{"disambiguationData":[OSD([subQ2])]});Q41=makeQuery(id+"F8.boolean.opBoolean","SPLIT",EDGE,{"disambiguationData":[topologyDisambiguationEdgeConnected([subQ3,subQ1]),TD([makeQuery(id+"F8.opExtrude","SWEPT_FACE",FACE,{"disambiguationData":[OSD([sQuery(id+"F7.wireOp",EDGE,"E103.right")])]})])],"derivedFrom":makeQuery(id+"F6.opExtrude","SWEPT_EDGE",EDGE,{"disambiguationData":[OSD([subQ2,subQ0])]})});}
            var Q42;
            {var subQ0=sQuery(id+"F5.wireOp",EDGE,"E102.trimOffspring");var subQ1=makeQuery(id+"F6.opExtrude","SWEPT_FACE",FACE,{"disambiguationData":[OSD([subQ0])]});var subQ2=sQuery(id+"F5.wireOp",EDGE,"E101");var subQ3=makeQuery(id+"F6.opExtrude","SWEPT_FACE",FACE,{"disambiguationData":[OSD([subQ2])]});Q42=makeQuery(id+"F8.boolean.opBoolean","SPLIT",EDGE,{"disambiguationData":[topologyDisambiguationEdgeConnected([subQ3,subQ1]),TD([makeQuery(id+"F8.opExtrude","SWEPT_FACE",FACE,{"disambiguationData":[OSD([sQuery(id+"F7.wireOp",EDGE,"E106.1.0.0")])]})])],"derivedFrom":makeQuery(id+"F6.opExtrude","SWEPT_EDGE",EDGE,{"disambiguationData":[OSD([subQ2,subQ0])]})});}
            var Q43;
            {var subQ0=sQuery(id+"F5.wireOp",EDGE,"E101");Q43=makeQuery(id+"F8.boolean.opBoolean","SPLIT",EDGE,{"disambiguationData":[topologyDisambiguationEdgeConnected([makeQuery(id+"F6.opExtrude","SWEPT_FACE",FACE,{"disambiguationData":[OSD([subQ0])]}),makeQuery(id+"F8.opExtrude","SWEPT_FACE",FACE,{"disambiguationData":[OSD([sQuery(id+"F7.wireOp",EDGE,"E106.2.0.2")])]})])],"derivedFrom":makeQuery(id+"F6.opExtrude","SWEPT_EDGE",EDGE,{"disambiguationData":[OSD([subQ0,sQuery(id+"F5.wireOp",EDGE,"E102.trimOffspring")])]})});}
            var Q44;
            {var subQ0=sQuery(id+"F5.wireOp",EDGE,"E102.trimOffspring");var subQ1=makeQuery(id+"F6.opExtrude","SWEPT_FACE",FACE,{"disambiguationData":[OSD([subQ0])]});var subQ2=sQuery(id+"F5.wireOp",EDGE,"E101");var subQ3=makeQuery(id+"F6.opExtrude","SWEPT_FACE",FACE,{"disambiguationData":[OSD([subQ2])]});Q44=makeQuery(id+"F8.boolean.opBoolean","SPLIT",EDGE,{"disambiguationData":[topologyDisambiguationEdgeConnected([subQ3,subQ1]),TD([makeQuery(id+"F8.opExtrude","SWEPT_FACE",FACE,{"disambiguationData":[OSD([sQuery(id+"F7.wireOp",EDGE,"E103.left")])]})])],"derivedFrom":makeQuery(id+"F6.opExtrude","SWEPT_EDGE",EDGE,{"disambiguationData":[OSD([subQ2,subQ0])]})});}
            var Q45;
            {var subQ0=sQuery(id+"F5.wireOp",EDGE,"E100");var subQ1=makeQuery(id+"F6.opExtrude","SWEPT_FACE",FACE,{"disambiguationData":[OSD([subQ0])]});var subQ2=sQuery(id+"F5.wireOp",EDGE,"E99");var subQ3=makeQuery(id+"F6.opExtrude","SWEPT_FACE",FACE,{"disambiguationData":[OSD([subQ2])]});Q45=makeQuery(id+"F8.boolean.opBoolean","SPLIT",EDGE,{"disambiguationData":[topologyDisambiguationEdgeConnected([subQ3,subQ1]),TD([makeQuery(id+"F8.opExtrude","SWEPT_FACE",FACE,{"disambiguationData":[OSD([sQuery(id+"F7.wireOp",EDGE,"E106.1.0.7")])]})])],"derivedFrom":makeQuery(id+"F6.opExtrude","SWEPT_EDGE",EDGE,{"disambiguationData":[OSD([subQ2,subQ0])]})});}
            var Q46;
            Q46=makeQuery(id+"F8.boolean.opBoolean","INTERSECT",EDGE,{"derivedFrom":[makeQuery(id+"F6.opExtrude","SWEPT_FACE",FACE,{"disambiguationData":[OSD([sQuery(id+"F5.wireOp",EDGE,"E99")])]}),makeQuery(id+"F8.opExtrude","SWEPT_FACE",FACE,{"disambiguationData":[OSD([sQuery(id+"F7.wireOp",EDGE,"E106.1.0.7")])]})]});
            var Q47;
            Q47=makeQuery(id+"F8.boolean.opBoolean","COPY",EDGE,{"derivedFrom":makeQuery(id+"F8.opExtrude","SWEPT_EDGE",EDGE,{"disambiguationData":[OSD([sQuery(id+"F7.wireOp",EDGE,"E106.2.0.4"),sQuery(id+"F7.wireOp",EDGE,"E106.2.0.7")])]})});
            var Q48;
            {var subQ0=sQuery(id+"F5.wireOp",EDGE,"E100");Q48=makeQuery(id+"F8.boolean.opBoolean","SPLIT",EDGE,{"disambiguationData":[topologyDisambiguationEdgeConnected([makeQuery(id+"F6.opExtrude","SWEPT_FACE",FACE,{"disambiguationData":[OSD([subQ0])]}),makeQuery(id+"F8.opExtrude","SWEPT_FACE",FACE,{"disambiguationData":[OSD([sQuery(id+"F7.wireOp",EDGE,"E106.1.0.2")])]})])],"derivedFrom":makeQuery(id+"F6.opExtrude","SWEPT_EDGE",EDGE,{"disambiguationData":[OSD([subQ0,sQuery(id+"F5.wireOp",EDGE,"E102.trimOffspring")])]})});}
            var Q49;
            Q49=makeQuery(id+"F8.boolean.opBoolean","COPY",EDGE,{"derivedFrom":makeQuery(id+"F8.opExtrude","SWEPT_EDGE",EDGE,{"disambiguationData":[OSD([sQuery(id+"F7.wireOp",EDGE,"E106.1.0.4"),sQuery(id+"F7.wireOp",EDGE,"E106.1.0.5")])]})});
            var Q50;
            {var subQ0=sQuery(id+"F5.wireOp",EDGE,"E99");var subQ1=makeQuery(id+"F6.opExtrude","SWEPT_FACE",FACE,{"disambiguationData":[OSD([subQ0])]});var subQ2=sQuery(id+"F5.wireOp",EDGE,"E100");var subQ3=makeQuery(id+"F6.opExtrude","SWEPT_FACE",FACE,{"disambiguationData":[OSD([subQ2])]});Q50=makeQuery(id+"F8.boolean.opBoolean","SPLIT",EDGE,{"disambiguationData":[topologyDisambiguationEdgeConnected([subQ1,subQ3]),TD([makeQuery(id+"F8.opExtrude","SWEPT_FACE",FACE,{"disambiguationData":[OSD([sQuery(id+"F7.wireOp",EDGE,"E104.left")])]})])],"derivedFrom":makeQuery(id+"F6.opExtrude","SWEPT_EDGE",EDGE,{"disambiguationData":[OSD([subQ0,subQ2])]})});}
            var Q51;
            Q51=makeQuery(id+"F8.boolean.opBoolean","INTERSECT",EDGE,{"derivedFrom":[makeQuery(id+"F6.opExtrude","SWEPT_FACE",FACE,{"disambiguationData":[OSD([sQuery(id+"F5.wireOp",EDGE,"E99")])]}),makeQuery(id+"F8.opExtrude","SWEPT_FACE",FACE,{"disambiguationData":[OSD([sQuery(id+"F7.wireOp",EDGE,"E105.1.0.0")])]})]});
            var Q52;
            Q52=makeQuery(id+"F8.boolean.opBoolean","COPY",EDGE,{"derivedFrom":makeQuery(id+"F8.opExtrude","SWEPT_EDGE",EDGE,{"disambiguationData":[OSD([sQuery(id+"F7.wireOp",EDGE,"E106.1.0.4"),sQuery(id+"F7.wireOp",EDGE,"E106.1.0.7")])]})});
            var Q53;
            Q53=makeQuery(id+"F8.boolean.opBoolean","COPY",EDGE,{"derivedFrom":makeQuery(id+"F8.opExtrude","SWEPT_EDGE",EDGE,{"disambiguationData":[OSD([sQuery(id+"F7.wireOp",EDGE,"E103.bottom"),sQuery(id+"F7.wireOp",EDGE,"E103.left")])]})});
            var Q54;
            Q54=makeQuery(id+"F8.boolean.opBoolean","COPY",EDGE,{"derivedFrom":makeQuery(id+"F8.opExtrude","SWEPT_EDGE",EDGE,{"disambiguationData":[OSD([sQuery(id+"F7.wireOp",EDGE,"E104.left"),sQuery(id+"F7.wireOp",EDGE,"E104.top")])]})});
            var Q55;
            {var subQ0=sQuery(id+"F5.wireOp",EDGE,"E101");Q55=makeQuery(id+"F8.boolean.opBoolean","SPLIT",EDGE,{"disambiguationData":[topologyDisambiguationEdgeConnected([makeQuery(id+"F6.opExtrude","SWEPT_FACE",FACE,{"disambiguationData":[OSD([subQ0])]}),makeQuery(id+"F8.opExtrude","SWEPT_FACE",FACE,{"disambiguationData":[OSD([sQuery(id+"F7.wireOp",EDGE,"E105.1.0.2")])]})])],"derivedFrom":makeQuery(id+"F6.opExtrude","SWEPT_EDGE",EDGE,{"disambiguationData":[OSD([sQuery(id+"F5.wireOp",EDGE,"E99"),subQ0])]})});}
            var Q56;
            {var subQ0=sQuery(id+"F5.wireOp",EDGE,"E101");Q56=makeQuery(id+"F8.boolean.opBoolean","SPLIT",EDGE,{"disambiguationData":[topologyDisambiguationEdgeConnected([makeQuery(id+"F6.opExtrude","SWEPT_FACE",FACE,{"disambiguationData":[OSD([subQ0])]}),makeQuery(id+"F8.opExtrude","SWEPT_FACE",FACE,{"disambiguationData":[OSD([sQuery(id+"F7.wireOp",EDGE,"E106.1.0.4")])]})])],"derivedFrom":makeQuery(id+"F6.opExtrude","SWEPT_EDGE",EDGE,{"disambiguationData":[OSD([sQuery(id+"F5.wireOp",EDGE,"E99"),subQ0])]})});}
            var Q57;
            {var subQ0=sQuery(id+"F5.wireOp",EDGE,"E102.trimOffspring");var subQ1=makeQuery(id+"F6.opExtrude","SWEPT_FACE",FACE,{"disambiguationData":[OSD([subQ0])]});var subQ2=sQuery(id+"F5.wireOp",EDGE,"E100");var subQ3=makeQuery(id+"F6.opExtrude","SWEPT_FACE",FACE,{"disambiguationData":[OSD([subQ2])]});Q57=makeQuery(id+"F8.boolean.opBoolean","SPLIT",EDGE,{"disambiguationData":[topologyDisambiguationEdgeConnected([subQ3,subQ1]),TD([makeQuery(id+"F8.opExtrude","SWEPT_FACE",FACE,{"disambiguationData":[OSD([sQuery(id+"F7.wireOp",EDGE,"E103.right")])]})])],"derivedFrom":makeQuery(id+"F6.opExtrude","SWEPT_EDGE",EDGE,{"disambiguationData":[OSD([subQ2,subQ0])]})});}
            var Q58;
            Q58=makeQuery(id+"F8.boolean.opBoolean","COPY",EDGE,{"derivedFrom":makeQuery(id+"F8.opExtrude","SWEPT_EDGE",EDGE,{"disambiguationData":[OSD([sQuery(id+"F7.wireOp",EDGE,"E105.1.0.0"),sQuery(id+"F7.wireOp",EDGE,"E105.1.0.2")])]})});
            var Q59;
            {var subQ0=sQuery(id+"F5.wireOp",EDGE,"E102.trimOffspring");var subQ1=makeQuery(id+"F6.opExtrude","SWEPT_FACE",FACE,{"disambiguationData":[OSD([subQ0])]});var subQ2=sQuery(id+"F5.wireOp",EDGE,"E101");var subQ3=makeQuery(id+"F6.opExtrude","SWEPT_FACE",FACE,{"disambiguationData":[OSD([subQ2])]});Q59=makeQuery(id+"F8.boolean.opBoolean","SPLIT",EDGE,{"disambiguationData":[topologyDisambiguationEdgeConnected([subQ3,subQ1]),TD([makeQuery(id+"F8.opExtrude","SWEPT_FACE",FACE,{"disambiguationData":[OSD([sQuery(id+"F7.wireOp",EDGE,"E105.2.0.5")])]})])],"derivedFrom":makeQuery(id+"F6.opExtrude","SWEPT_EDGE",EDGE,{"disambiguationData":[OSD([subQ2,subQ0])]})});}
            var Q60;
            Q60=makeQuery(id+"F8.boolean.opBoolean","COPY",EDGE,{"derivedFrom":makeQuery(id+"F8.opExtrude","SWEPT_EDGE",EDGE,{"disambiguationData":[OSD([sQuery(id+"F7.wireOp",EDGE,"E105.1.0.2"),sQuery(id+"F7.wireOp",EDGE,"E105.1.0.3")])]})});
            var Q61;
            Q61=makeQuery(id+"F8.boolean.opBoolean","INTERSECT",EDGE,{"derivedFrom":[makeQuery(id+"F6.opExtrude","SWEPT_FACE",FACE,{"disambiguationData":[OSD([sQuery(id+"F5.wireOp",EDGE,"E99")])]}),makeQuery(id+"F8.opExtrude","SWEPT_FACE",FACE,{"disambiguationData":[OSD([sQuery(id+"F7.wireOp",EDGE,"E105.2.0.0")])]})]});
            var Q62;
            {var subQ0=sQuery(id+"F5.wireOp",EDGE,"E102.trimOffspring");var subQ1=makeQuery(id+"F6.opExtrude","SWEPT_FACE",FACE,{"disambiguationData":[OSD([subQ0])]});var subQ2=sQuery(id+"F5.wireOp",EDGE,"E100");var subQ3=makeQuery(id+"F6.opExtrude","SWEPT_FACE",FACE,{"disambiguationData":[OSD([subQ2])]});Q62=makeQuery(id+"F8.boolean.opBoolean","SPLIT",EDGE,{"disambiguationData":[topologyDisambiguationEdgeConnected([subQ3,subQ1]),TD([makeQuery(id+"F8.opExtrude","SWEPT_FACE",FACE,{"disambiguationData":[OSD([sQuery(id+"F7.wireOp",EDGE,"E103.left")])]})])],"derivedFrom":makeQuery(id+"F6.opExtrude","SWEPT_EDGE",EDGE,{"disambiguationData":[OSD([subQ2,subQ0])]})});}
            var Q63;
            Q63=makeQuery(id+"F8.boolean.opBoolean","COPY",EDGE,{"derivedFrom":makeQuery(id+"F8.opExtrude","SWEPT_EDGE",EDGE,{"disambiguationData":[OSD([sQuery(id+"F7.wireOp",EDGE,"E105.1.0.5"),sQuery(id+"F7.wireOp",EDGE,"E105.1.0.7")])]})});
            var Q64;
            {var subQ0=sQuery(id+"F5.wireOp",EDGE,"E100");Q64=makeQuery(id+"F8.boolean.opBoolean","SPLIT",EDGE,{"disambiguationData":[topologyDisambiguationEdgeConnected([makeQuery(id+"F6.opExtrude","SWEPT_FACE",FACE,{"disambiguationData":[OSD([subQ0])]}),makeQuery(id+"F8.opExtrude","SWEPT_FACE",FACE,{"disambiguationData":[OSD([sQuery(id+"F7.wireOp",EDGE,"E106.2.0.2")])]})])],"derivedFrom":makeQuery(id+"F6.opExtrude","SWEPT_EDGE",EDGE,{"disambiguationData":[OSD([subQ0,sQuery(id+"F5.wireOp",EDGE,"E102.trimOffspring")])]})});}
            var Q65;
            {var subQ0=sQuery(id+"F5.wireOp",EDGE,"E101");Q65=makeQuery(id+"F8.boolean.opBoolean","SPLIT",EDGE,{"disambiguationData":[topologyDisambiguationEdgeConnected([makeQuery(id+"F6.opExtrude","SWEPT_FACE",FACE,{"disambiguationData":[OSD([subQ0])]}),makeQuery(id+"F8.opExtrude","SWEPT_FACE",FACE,{"disambiguationData":[OSD([sQuery(id+"F7.wireOp",EDGE,"E105.2.0.2")])]})])],"derivedFrom":makeQuery(id+"F6.opExtrude","SWEPT_EDGE",EDGE,{"disambiguationData":[OSD([sQuery(id+"F5.wireOp",EDGE,"E99"),subQ0])]})});}
            var Q66;
            {var subQ0=sQuery(id+"F5.wireOp",EDGE,"E101");Q66=makeQuery(id+"F8.boolean.opBoolean","SPLIT",EDGE,{"disambiguationData":[topologyDisambiguationEdgeConnected([makeQuery(id+"F6.opExtrude","SWEPT_FACE",FACE,{"disambiguationData":[OSD([subQ0])]}),makeQuery(id+"F8.opExtrude","SWEPT_FACE",FACE,{"disambiguationData":[OSD([sQuery(id+"F7.wireOp",EDGE,"E106.2.0.4")])]})])],"derivedFrom":makeQuery(id+"F6.opExtrude","SWEPT_EDGE",EDGE,{"disambiguationData":[OSD([sQuery(id+"F5.wireOp",EDGE,"E99"),subQ0])]})});}
            var Q67;
            Q67=makeQuery(id+"F6.opExtrude","CAP_EDGE",EDGE,{"disambiguationData":[OSD([sQuery(id+"F5.wireOp",EDGE,"E101")])],"isStart":false});
            var Q68;
            Q68=makeQuery(id+"F6.opExtrude","CAP_EDGE",EDGE,{"disambiguationData":[OSD([sQuery(id+"F5.wireOp",EDGE,"E101")])],"isStart":true});
            var Q69;
            Q69=makeQuery(id+"F6.opExtrude","CAP_EDGE",EDGE,{"disambiguationData":[OSD([sQuery(id+"F5.wireOp",EDGE,"E100")])],"isStart":false});
            var Q70;
            Q70=makeQuery(id+"F6.opExtrude","CAP_EDGE",EDGE,{"disambiguationData":[OSD([sQuery(id+"F5.wireOp",EDGE,"E99")])],"isStart":true});
            var Q71;
            Q71=makeQuery(id+"F8.boolean.opBoolean","INTERSECT",EDGE,{"derivedFrom":[makeQuery(id+"F6.opExtrude","SWEPT_FACE",FACE,{"disambiguationData":[OSD([sQuery(id+"F5.wireOp",EDGE,"E99")])]}),makeQuery(id+"F8.opExtrude","SWEPT_FACE",FACE,{"disambiguationData":[OSD([sQuery(id+"F7.wireOp",EDGE,"E106.2.0.7")])]})]});
            var Q72;
            {var subQ0=sQuery(id+"F5.wireOp",EDGE,"E102.trimOffspring");var subQ1=makeQuery(id+"F6.opExtrude","SWEPT_FACE",FACE,{"disambiguationData":[OSD([subQ0])]});var subQ2=sQuery(id+"F5.wireOp",EDGE,"E100");var subQ3=makeQuery(id+"F6.opExtrude","SWEPT_FACE",FACE,{"disambiguationData":[OSD([subQ2])]});Q72=makeQuery(id+"F8.boolean.opBoolean","SPLIT",EDGE,{"disambiguationData":[topologyDisambiguationEdgeConnected([subQ3,subQ1]),TD([makeQuery(id+"F8.opExtrude","SWEPT_FACE",FACE,{"disambiguationData":[OSD([sQuery(id+"F7.wireOp",EDGE,"E106.2.0.0")])]})])],"derivedFrom":makeQuery(id+"F6.opExtrude","SWEPT_EDGE",EDGE,{"disambiguationData":[OSD([subQ2,subQ0])]})});}
            var Q73;
            Q73=makeQuery(id+"F8.boolean.opBoolean","INTERSECT",EDGE,{"derivedFrom":[makeQuery(id+"F6.opExtrude","SWEPT_FACE",FACE,{"disambiguationData":[OSD([sQuery(id+"F5.wireOp",EDGE,"E99")])]}),makeQuery(id+"F8.opExtrude","SWEPT_FACE",FACE,{"disambiguationData":[OSD([sQuery(id+"F7.wireOp",EDGE,"E104.right")])]})]});
            var Q74;
            {var subQ0=sQuery(id+"F5.wireOp",EDGE,"E102.trimOffspring");var subQ1=makeQuery(id+"F6.opExtrude","SWEPT_FACE",FACE,{"disambiguationData":[OSD([subQ0])]});var subQ2=sQuery(id+"F5.wireOp",EDGE,"E100");var subQ3=makeQuery(id+"F6.opExtrude","SWEPT_FACE",FACE,{"disambiguationData":[OSD([subQ2])]});Q74=makeQuery(id+"F8.boolean.opBoolean","SPLIT",EDGE,{"disambiguationData":[topologyDisambiguationEdgeConnected([subQ3,subQ1]),TD([makeQuery(id+"F8.opExtrude","SWEPT_FACE",FACE,{"disambiguationData":[OSD([sQuery(id+"F7.wireOp",EDGE,"E105.2.0.5")])]})])],"derivedFrom":makeQuery(id+"F6.opExtrude","SWEPT_EDGE",EDGE,{"disambiguationData":[OSD([subQ2,subQ0])]})});}
            var Q75;
            Q75=makeQuery(id+"F8.boolean.opBoolean","INTERSECT",EDGE,{"derivedFrom":[makeQuery(id+"F6.opExtrude","SWEPT_FACE",FACE,{"disambiguationData":[OSD([sQuery(id+"F5.wireOp",EDGE,"E99")])]}),makeQuery(id+"F8.opExtrude","SWEPT_FACE",FACE,{"disambiguationData":[OSD([sQuery(id+"F7.wireOp",EDGE,"E105.1.0.3")])]})]});
            var Q76;
            Q76=makeQuery(id+"F8.boolean.opBoolean","COPY",EDGE,{"derivedFrom":makeQuery(id+"F8.opExtrude","SWEPT_EDGE",EDGE,{"disambiguationData":[OSD([sQuery(id+"F7.wireOp",EDGE,"E106.1.0.2"),sQuery(id+"F7.wireOp",EDGE,"E106.1.0.3")])]})});
            var Q77;
            {var subQ0=sQuery(id+"F5.wireOp",EDGE,"E100");Q77=makeQuery(id+"F8.boolean.opBoolean","SPLIT",EDGE,{"disambiguationData":[topologyDisambiguationEdgeConnected([makeQuery(id+"F6.opExtrude","SWEPT_FACE",FACE,{"disambiguationData":[OSD([subQ0])]}),makeQuery(id+"F8.opExtrude","SWEPT_FACE",FACE,{"disambiguationData":[OSD([sQuery(id+"F7.wireOp",EDGE,"E103.bottom")])]})])],"derivedFrom":makeQuery(id+"F6.opExtrude","SWEPT_EDGE",EDGE,{"disambiguationData":[OSD([subQ0,sQuery(id+"F5.wireOp",EDGE,"E102.trimOffspring")])]})});}
            var Q78;
            {var subQ0=sQuery(id+"F5.wireOp",EDGE,"E100");Q78=makeQuery(id+"F8.boolean.opBoolean","SPLIT",EDGE,{"disambiguationData":[topologyDisambiguationEdgeConnected([makeQuery(id+"F6.opExtrude","SWEPT_FACE",FACE,{"disambiguationData":[OSD([subQ0])]}),makeQuery(id+"F8.opExtrude","SWEPT_FACE",FACE,{"disambiguationData":[OSD([sQuery(id+"F7.wireOp",EDGE,"E105.2.0.7")])]})])],"derivedFrom":makeQuery(id+"F6.opExtrude","SWEPT_EDGE",EDGE,{"disambiguationData":[OSD([subQ0,sQuery(id+"F5.wireOp",EDGE,"E102.trimOffspring")])]})});}
            var Q79;
            Q79=makeQuery(id+"F8.boolean.opBoolean","INTERSECT",EDGE,{"derivedFrom":[makeQuery(id+"F6.opExtrude","SWEPT_FACE",FACE,{"disambiguationData":[OSD([sQuery(id+"F5.wireOp",EDGE,"E99")])]}),makeQuery(id+"F8.opExtrude","SWEPT_FACE",FACE,{"disambiguationData":[OSD([sQuery(id+"F7.wireOp",EDGE,"E105.2.0.3")])]})]});
            var Q80;
            {var subQ0=sQuery(id+"F5.wireOp",EDGE,"E101");Q80=makeQuery(id+"F8.boolean.opBoolean","SPLIT",EDGE,{"disambiguationData":[topologyDisambiguationEdgeConnected([makeQuery(id+"F6.opExtrude","SWEPT_FACE",FACE,{"disambiguationData":[OSD([subQ0])]}),makeQuery(id+"F8.opExtrude","SWEPT_FACE",FACE,{"disambiguationData":[OSD([sQuery(id+"F7.wireOp",EDGE,"E105.1.0.7")])]})])],"derivedFrom":makeQuery(id+"F6.opExtrude","SWEPT_EDGE",EDGE,{"disambiguationData":[OSD([subQ0,sQuery(id+"F5.wireOp",EDGE,"E102.trimOffspring")])]})});}
            var Q81;
            {var subQ0=sQuery(id+"F5.wireOp",EDGE,"E100");Q81=makeQuery(id+"F8.boolean.opBoolean","SPLIT",EDGE,{"disambiguationData":[topologyDisambiguationEdgeConnected([makeQuery(id+"F6.opExtrude","SWEPT_FACE",FACE,{"disambiguationData":[OSD([subQ0])]}),makeQuery(id+"F8.opExtrude","SWEPT_FACE",FACE,{"disambiguationData":[OSD([sQuery(id+"F7.wireOp",EDGE,"E105.1.0.2")])]})])],"derivedFrom":makeQuery(id+"F6.opExtrude","SWEPT_EDGE",EDGE,{"disambiguationData":[OSD([sQuery(id+"F5.wireOp",EDGE,"E99"),subQ0])]})});}
            var Q82;
            Q82=makeQuery(id+"F8.boolean.opBoolean","COPY",EDGE,{"derivedFrom":makeQuery(id+"F8.opExtrude","SWEPT_EDGE",EDGE,{"disambiguationData":[OSD([sQuery(id+"F7.wireOp",EDGE,"E106.2.0.4"),sQuery(id+"F7.wireOp",EDGE,"E106.2.0.5")])]})});
            var Q83;
            Q83=makeQuery(id+"F8.boolean.opBoolean","INTERSECT",EDGE,{"derivedFrom":[makeQuery(id+"F6.opExtrude","SWEPT_FACE",FACE,{"disambiguationData":[OSD([sQuery(id+"F5.wireOp",EDGE,"E99")])]}),makeQuery(id+"F8.opExtrude","SWEPT_FACE",FACE,{"disambiguationData":[OSD([sQuery(id+"F7.wireOp",EDGE,"E106.1.0.5")])]})]});
            var Q84;
            {var subQ0=sQuery(id+"F5.wireOp",EDGE,"E100");Q84=makeQuery(id+"F8.boolean.opBoolean","SPLIT",EDGE,{"disambiguationData":[topologyDisambiguationEdgeConnected([makeQuery(id+"F6.opExtrude","SWEPT_FACE",FACE,{"disambiguationData":[OSD([subQ0])]}),makeQuery(id+"F8.opExtrude","SWEPT_FACE",FACE,{"disambiguationData":[OSD([sQuery(id+"F7.wireOp",EDGE,"E104.top")])]})])],"derivedFrom":makeQuery(id+"F6.opExtrude","SWEPT_EDGE",EDGE,{"disambiguationData":[OSD([sQuery(id+"F5.wireOp",EDGE,"E99"),subQ0])]})});}
            var Q85;
            Q85=makeQuery(id+"F8.boolean.opBoolean","COPY",EDGE,{"derivedFrom":makeQuery(id+"F8.opExtrude","SWEPT_EDGE",EDGE,{"disambiguationData":[OSD([sQuery(id+"F7.wireOp",EDGE,"E106.2.0.2"),sQuery(id+"F7.wireOp",EDGE,"E106.2.0.3")])]})});
            var Q86;
            {var subQ0=sQuery(id+"F5.wireOp",EDGE,"E100");Q86=makeQuery(id+"F8.boolean.opBoolean","SPLIT",EDGE,{"disambiguationData":[topologyDisambiguationEdgeConnected([makeQuery(id+"F6.opExtrude","SWEPT_FACE",FACE,{"disambiguationData":[OSD([subQ0])]}),makeQuery(id+"F8.opExtrude","SWEPT_FACE",FACE,{"disambiguationData":[OSD([sQuery(id+"F7.wireOp",EDGE,"E105.2.0.2")])]})])],"derivedFrom":makeQuery(id+"F6.opExtrude","SWEPT_EDGE",EDGE,{"disambiguationData":[OSD([sQuery(id+"F5.wireOp",EDGE,"E99"),subQ0])]})});}
            var Q87;
            {var subQ0=sQuery(id+"F5.wireOp",EDGE,"E100");Q87=makeQuery(id+"F8.boolean.opBoolean","SPLIT",EDGE,{"disambiguationData":[topologyDisambiguationEdgeConnected([makeQuery(id+"F6.opExtrude","SWEPT_FACE",FACE,{"disambiguationData":[OSD([subQ0])]}),makeQuery(id+"F8.opExtrude","SWEPT_FACE",FACE,{"disambiguationData":[OSD([sQuery(id+"F7.wireOp",EDGE,"E106.1.0.4")])]})])],"derivedFrom":makeQuery(id+"F6.opExtrude","SWEPT_EDGE",EDGE,{"disambiguationData":[OSD([sQuery(id+"F5.wireOp",EDGE,"E99"),subQ0])]})});}
            var Q88;
            Q88=makeQuery(id+"F6.opExtrude","CAP_EDGE",EDGE,{"disambiguationData":[OSD([sQuery(id+"F5.wireOp",EDGE,"E100")])],"isStart":true});
            var Q89;
            Q89=makeQuery(id+"F8.boolean.opBoolean","INTERSECT",EDGE,{"derivedFrom":[makeQuery(id+"F6.opExtrude","SWEPT_FACE",FACE,{"disambiguationData":[OSD([sQuery(id+"F5.wireOp",EDGE,"E99")])]}),makeQuery(id+"F8.opExtrude","SWEPT_FACE",FACE,{"disambiguationData":[OSD([sQuery(id+"F7.wireOp",EDGE,"E104.left")])]})]});
            var Q90;
            Q90=makeQuery(id+"F8.boolean.opBoolean","INTERSECT",EDGE,{"derivedFrom":[makeQuery(id+"F6.opExtrude","SWEPT_FACE",FACE,{"disambiguationData":[OSD([sQuery(id+"F5.wireOp",EDGE,"E99")])]}),makeQuery(id+"F8.opExtrude","SWEPT_FACE",FACE,{"disambiguationData":[OSD([sQuery(id+"F7.wireOp",EDGE,"E106.2.0.5")])]})]});
            var Q91;
            {var subQ0=sQuery(id+"F5.wireOp",EDGE,"E100");Q91=makeQuery(id+"F8.boolean.opBoolean","SPLIT",EDGE,{"disambiguationData":[topologyDisambiguationEdgeConnected([makeQuery(id+"F6.opExtrude","SWEPT_FACE",FACE,{"disambiguationData":[OSD([subQ0])]}),makeQuery(id+"F8.opExtrude","SWEPT_FACE",FACE,{"disambiguationData":[OSD([sQuery(id+"F7.wireOp",EDGE,"E106.2.0.4")])]})])],"derivedFrom":makeQuery(id+"F6.opExtrude","SWEPT_EDGE",EDGE,{"disambiguationData":[OSD([sQuery(id+"F5.wireOp",EDGE,"E99"),subQ0])]})});}
            fillet(context, id + "F9", {"entities" : qUnion([Q0, Q1, Q2, Q3, Q4, Q5, Q6, Q7, Q8, Q9, Q10, Q11, Q12, Q13, Q14, Q15, Q16, Q17, Q18, Q19, Q20, Q21, Q22, Q23, Q24, Q25, Q26, Q27, Q28, Q29, Q30, Q31, Q32, Q33, Q34, Q35, Q36, Q37, Q38, Q39, Q40, Q41, Q42, Q43, Q44, Q45, Q46, Q47, Q48, Q49, Q50, Q51, Q52, Q53, Q54, Q55, Q56, Q57, Q58, Q59, Q60, Q61, Q62, Q63, Q64, Q65, Q66, Q67, Q68, Q69, Q70, Q71, Q72, Q73, Q74, Q75, Q76, Q77, Q78, Q79, Q80, Q81, Q82, Q83, Q84, Q85, Q86, Q87, Q88, Q89, Q90, Q91]), "radius" : 1 * mm, "tangentPropagation" : true, "allowEdgeOverflow" : false});
        }
    });
